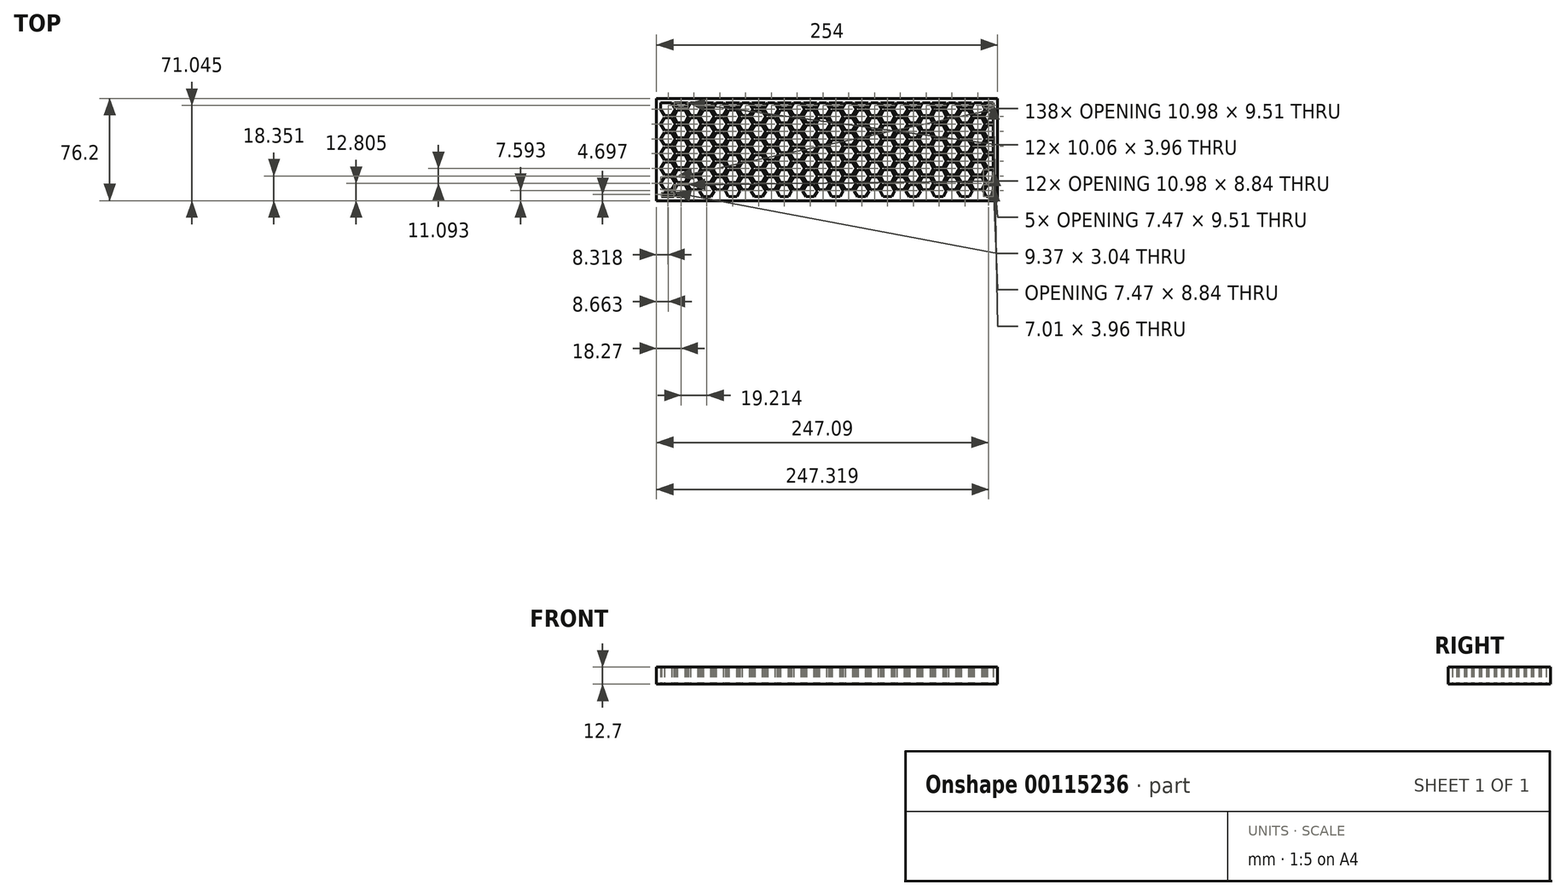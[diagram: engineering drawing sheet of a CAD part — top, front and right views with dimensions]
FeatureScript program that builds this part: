
annotation { "Feature Type Name" : "Feature", "Feature Type Description" : "" }
export const myFeature = defineFeature(function(context is Context, id is Id, definition is map)
    precondition{}
    {
        {
            var Q0;
            Q0=qCreatedBy(makeId("Top.planeOp"),FACE);
            var sketch = newSketch(context, id + "F0", { "sketchPlane" : qUnion([Q0])});
            skLineSegment(sketch, "E0.bottom", {"start": v(0, 0) * mm, "end": v(254, 0) * mm});
            skLineSegment(sketch, "E0.top", {"start": v(0, 76.2) * mm, "end": v(254, 76.2) * mm});
            skLineSegment(sketch, "E0.left", {"start": v(0, 0) * mm, "end": v(0, 76.2) * mm});
            skLineSegment(sketch, "E0.right", {"start": v(254, 0) * mm, "end": v(254, 76.2) * mm});
            skLineSegment(sketch, "E1.0", {"start": v(3.17, 73.02) * mm, "end": v(250.83, 73.02) * mm});
            skLineSegment(sketch, "E1.1", {"start": v(3.17, 3.17) * mm, "end": v(3.17, 73.03) * mm});
            skLineSegment(sketch, "E1.2", {"start": v(3.17, 3.17) * mm, "end": v(250.83, 3.17) * mm});
            skLineSegment(sketch, "E1.3", {"start": v(250.83, 3.17) * mm, "end": v(250.83, 73.03) * mm});
            skCircle(sketch, "E2.cCircle", {"center": v(8.66, 68.27) * mm, "radius": 4.75 * mm, "construction": true});
            skLineSegment(sketch, "E2.0", {"start": v(5.92, 73.02) * mm, "end": v(11.4, 73.02) * mm});
            skLineSegment(sketch, "E2.1", {"start": v(11.4, 73.02) * mm, "end": v(14.15, 68.27) * mm});
            skLineSegment(sketch, "E2.2", {"start": v(14.15, 68.27) * mm, "end": v(11.4, 63.52) * mm});
            skLineSegment(sketch, "E2.3", {"start": v(11.4, 63.52) * mm, "end": v(5.92, 63.52) * mm});
            skLineSegment(sketch, "E2.4", {"start": v(5.92, 63.52) * mm, "end": v(3.17, 68.27) * mm});
            skLineSegment(sketch, "E2.5", {"start": v(3.18, 68.27) * mm, "end": v(5.92, 73.02) * mm});
            skPoint(sketch, "E2.0.midPoint", {"position": v(8.66, 73.03) * mm});
            skPoint(sketch, "E3.0.midPoint", {"position": v(8.6, 62.03) * mm});
            skPoint(sketch, "E4.0.midPoint", {"position": v(12.97, 60.07) * mm});
            skCircle(sketch, "E5.cCircle", {"center": v(18.27, 62.73) * mm, "radius": 4.75 * mm, "construction": true});
            skLineSegment(sketch, "E5.0", {"start": v(15.53, 67.48) * mm, "end": v(21.01, 67.48) * mm});
            skLineSegment(sketch, "E5.1", {"start": v(21.01, 67.48) * mm, "end": v(23.76, 62.73) * mm});
            skLineSegment(sketch, "E5.2", {"start": v(23.76, 62.73) * mm, "end": v(21.01, 57.97) * mm});
            skLineSegment(sketch, "E5.3", {"start": v(21.01, 57.97) * mm, "end": v(15.53, 57.97) * mm});
            skLineSegment(sketch, "E5.4", {"start": v(15.53, 57.97) * mm, "end": v(12.78, 62.73) * mm});
            skLineSegment(sketch, "E5.5", {"start": v(12.78, 62.73) * mm, "end": v(15.53, 67.48) * mm});
            skPoint(sketch, "E5.0.midPoint", {"position": v(18.27, 67.48) * mm});
            skLineSegment(sketch, "E6.0.1.0", {"start": v(11.4, 61.93) * mm, "end": v(14.15, 57.18) * mm});
            skLineSegment(sketch, "E6.0.1.1", {"start": v(3.17, 57.18) * mm, "end": v(5.92, 61.93) * mm});
            skLineSegment(sketch, "E6.0.1.2", {"start": v(5.92, 52.43) * mm, "end": v(3.18, 57.18) * mm});
            skLineSegment(sketch, "E6.0.1.3", {"start": v(11.4, 52.43) * mm, "end": v(5.92, 52.43) * mm});
            skLineSegment(sketch, "E6.0.1.4", {"start": v(14.15, 57.18) * mm, "end": v(11.4, 52.43) * mm});
            skLineSegment(sketch, "E6.0.1.5", {"start": v(12.78, 51.63) * mm, "end": v(15.53, 56.38) * mm});
            skLineSegment(sketch, "E6.0.1.6", {"start": v(15.53, 46.88) * mm, "end": v(12.78, 51.63) * mm});
            skLineSegment(sketch, "E6.0.1.7", {"start": v(21.01, 46.88) * mm, "end": v(15.53, 46.88) * mm});
            skLineSegment(sketch, "E6.0.1.8", {"start": v(23.76, 51.63) * mm, "end": v(21.01, 46.88) * mm});
            skLineSegment(sketch, "E6.0.1.9", {"start": v(21.01, 56.38) * mm, "end": v(23.76, 51.63) * mm});
            skLineSegment(sketch, "E6.0.1.10", {"start": v(15.53, 56.38) * mm, "end": v(21.01, 56.38) * mm});
            skLineSegment(sketch, "E6.0.1.11", {"start": v(5.92, 61.93) * mm, "end": v(11.4, 61.93) * mm});
            skLineSegment(sketch, "E6.0.2.0", {"start": v(11.4, 50.84) * mm, "end": v(14.15, 46.09) * mm});
            skLineSegment(sketch, "E6.0.2.1", {"start": v(3.17, 46.09) * mm, "end": v(5.92, 50.84) * mm});
            skLineSegment(sketch, "E6.0.2.2", {"start": v(5.92, 41.33) * mm, "end": v(3.18, 46.09) * mm});
            skLineSegment(sketch, "E6.0.2.3", {"start": v(11.4, 41.33) * mm, "end": v(5.92, 41.33) * mm});
            skLineSegment(sketch, "E6.0.2.4", {"start": v(14.15, 46.09) * mm, "end": v(11.4, 41.33) * mm});
            skLineSegment(sketch, "E6.0.2.5", {"start": v(12.78, 40.54) * mm, "end": v(15.53, 45.3) * mm});
            skLineSegment(sketch, "E6.0.2.6", {"start": v(15.53, 35.79) * mm, "end": v(12.78, 40.54) * mm});
            skLineSegment(sketch, "E6.0.2.7", {"start": v(21.01, 35.79) * mm, "end": v(15.53, 35.79) * mm});
            skLineSegment(sketch, "E6.0.2.8", {"start": v(23.76, 40.54) * mm, "end": v(21.01, 35.79) * mm});
            skLineSegment(sketch, "E6.0.2.9", {"start": v(21.01, 45.3) * mm, "end": v(23.76, 40.54) * mm});
            skLineSegment(sketch, "E6.0.2.10", {"start": v(15.53, 45.3) * mm, "end": v(21.01, 45.3) * mm});
            skLineSegment(sketch, "E6.0.2.11", {"start": v(5.92, 50.84) * mm, "end": v(11.4, 50.84) * mm});
            skLineSegment(sketch, "E6.0.3.0", {"start": v(11.4, 39.74) * mm, "end": v(14.15, 35) * mm});
            skLineSegment(sketch, "E6.0.3.1", {"start": v(3.17, 35) * mm, "end": v(5.92, 39.74) * mm});
            skLineSegment(sketch, "E6.0.3.2", {"start": v(5.92, 30.24) * mm, "end": v(3.18, 35) * mm});
            skLineSegment(sketch, "E6.0.3.3", {"start": v(11.4, 30.24) * mm, "end": v(5.92, 30.24) * mm});
            skLineSegment(sketch, "E6.0.3.4", {"start": v(14.15, 35) * mm, "end": v(11.4, 30.24) * mm});
            skLineSegment(sketch, "E6.0.3.5", {"start": v(12.78, 29.44) * mm, "end": v(15.53, 34.2) * mm});
            skLineSegment(sketch, "E6.0.3.6", {"start": v(15.53, 24.7) * mm, "end": v(12.78, 29.44) * mm});
            skLineSegment(sketch, "E6.0.3.7", {"start": v(21.01, 24.7) * mm, "end": v(15.53, 24.7) * mm});
            skLineSegment(sketch, "E6.0.3.8", {"start": v(23.76, 29.44) * mm, "end": v(21.01, 24.7) * mm});
            skLineSegment(sketch, "E6.0.3.9", {"start": v(21.01, 34.2) * mm, "end": v(23.76, 29.44) * mm});
            skLineSegment(sketch, "E6.0.3.10", {"start": v(15.53, 34.2) * mm, "end": v(21.01, 34.2) * mm});
            skLineSegment(sketch, "E6.0.3.11", {"start": v(5.92, 39.74) * mm, "end": v(11.4, 39.74) * mm});
            skLineSegment(sketch, "E6.0.4.0", {"start": v(11.4, 28.65) * mm, "end": v(14.15, 23.9) * mm});
            skLineSegment(sketch, "E6.0.4.1", {"start": v(3.17, 23.9) * mm, "end": v(5.92, 28.65) * mm});
            skLineSegment(sketch, "E6.0.4.2", {"start": v(5.92, 19.15) * mm, "end": v(3.18, 23.9) * mm});
            skLineSegment(sketch, "E6.0.4.3", {"start": v(11.4, 19.15) * mm, "end": v(5.92, 19.15) * mm});
            skLineSegment(sketch, "E6.0.4.4", {"start": v(14.15, 23.9) * mm, "end": v(11.4, 19.15) * mm});
            skLineSegment(sketch, "E6.0.4.5", {"start": v(12.78, 18.35) * mm, "end": v(15.53, 23.1) * mm});
            skLineSegment(sketch, "E6.0.4.6", {"start": v(15.53, 13.6) * mm, "end": v(12.78, 18.35) * mm});
            skLineSegment(sketch, "E6.0.4.7", {"start": v(21.01, 13.6) * mm, "end": v(15.53, 13.6) * mm});
            skLineSegment(sketch, "E6.0.4.8", {"start": v(23.76, 18.35) * mm, "end": v(21.01, 13.6) * mm});
            skLineSegment(sketch, "E6.0.4.9", {"start": v(21.01, 23.1) * mm, "end": v(23.76, 18.35) * mm});
            skLineSegment(sketch, "E6.0.4.10", {"start": v(15.53, 23.1) * mm, "end": v(21.01, 23.1) * mm});
            skLineSegment(sketch, "E6.0.4.11", {"start": v(5.92, 28.65) * mm, "end": v(11.4, 28.65) * mm});
            skLineSegment(sketch, "E6.0.5.0", {"start": v(11.4, 17.56) * mm, "end": v(14.15, 12.8) * mm});
            skLineSegment(sketch, "E6.0.5.1", {"start": v(3.18, 12.8) * mm, "end": v(5.92, 17.56) * mm});
            skLineSegment(sketch, "E6.0.5.2", {"start": v(5.92, 8.05) * mm, "end": v(3.18, 12.8) * mm});
            skLineSegment(sketch, "E6.0.5.3", {"start": v(11.4, 8.05) * mm, "end": v(5.92, 8.05) * mm});
            skLineSegment(sketch, "E6.0.5.4", {"start": v(14.15, 12.8) * mm, "end": v(11.4, 8.05) * mm});
            skLineSegment(sketch, "E6.0.5.5", {"start": v(12.78, 7.26) * mm, "end": v(15.53, 12.01) * mm});
            skLineSegment(sketch, "E6.0.5.6", {"start": v(15.53, 2.5) * mm, "end": v(12.78, 7.26) * mm});
            skLineSegment(sketch, "E6.0.5.7", {"start": v(21.01, 2.5) * mm, "end": v(15.53, 2.5) * mm});
            skLineSegment(sketch, "E6.0.5.8", {"start": v(23.76, 7.26) * mm, "end": v(21.01, 2.5) * mm});
            skLineSegment(sketch, "E6.0.5.9", {"start": v(21.01, 12.01) * mm, "end": v(23.76, 7.26) * mm});
            skLineSegment(sketch, "E6.0.5.10", {"start": v(15.53, 12.01) * mm, "end": v(21.01, 12.01) * mm});
            skLineSegment(sketch, "E6.0.5.11", {"start": v(5.92, 17.56) * mm, "end": v(11.4, 17.56) * mm});
            skLineSegment(sketch, "E6.1.0.0", {"start": v(30.62, 73.02) * mm, "end": v(33.37, 68.27) * mm});
            skLineSegment(sketch, "E6.1.0.1", {"start": v(22.39, 68.27) * mm, "end": v(25.13, 73.02) * mm});
            skLineSegment(sketch, "E6.1.0.2", {"start": v(25.13, 63.52) * mm, "end": v(22.39, 68.27) * mm});
            skLineSegment(sketch, "E6.1.0.3", {"start": v(30.62, 63.52) * mm, "end": v(25.13, 63.52) * mm});
            skLineSegment(sketch, "E6.1.0.4", {"start": v(33.37, 68.27) * mm, "end": v(30.62, 63.52) * mm});
            skLineSegment(sketch, "E6.1.0.5", {"start": v(32, 62.73) * mm, "end": v(34.74, 67.48) * mm});
            skLineSegment(sketch, "E6.1.0.6", {"start": v(34.74, 57.97) * mm, "end": v(32, 62.73) * mm});
            skLineSegment(sketch, "E6.1.0.7", {"start": v(40.23, 57.97) * mm, "end": v(34.74, 57.97) * mm});
            skLineSegment(sketch, "E6.1.0.8", {"start": v(42.97, 62.73) * mm, "end": v(40.23, 57.97) * mm});
            skLineSegment(sketch, "E6.1.0.9", {"start": v(40.23, 67.48) * mm, "end": v(42.97, 62.73) * mm});
            skLineSegment(sketch, "E6.1.0.10", {"start": v(34.74, 67.48) * mm, "end": v(40.23, 67.48) * mm});
            skLineSegment(sketch, "E6.1.0.11", {"start": v(25.13, 73.03) * mm, "end": v(30.62, 73.03) * mm});
            skLineSegment(sketch, "E6.1.1.0", {"start": v(30.62, 61.93) * mm, "end": v(33.37, 57.18) * mm});
            skLineSegment(sketch, "E6.1.1.1", {"start": v(22.39, 57.18) * mm, "end": v(25.13, 61.93) * mm});
            skLineSegment(sketch, "E6.1.1.2", {"start": v(25.13, 52.43) * mm, "end": v(22.39, 57.18) * mm});
            skLineSegment(sketch, "E6.1.1.3", {"start": v(30.62, 52.43) * mm, "end": v(25.13, 52.43) * mm});
            skLineSegment(sketch, "E6.1.1.4", {"start": v(33.37, 57.18) * mm, "end": v(30.62, 52.43) * mm});
            skLineSegment(sketch, "E6.1.1.5", {"start": v(32, 51.63) * mm, "end": v(34.74, 56.38) * mm});
            skLineSegment(sketch, "E6.1.1.6", {"start": v(34.74, 46.88) * mm, "end": v(32, 51.63) * mm});
            skLineSegment(sketch, "E6.1.1.7", {"start": v(40.23, 46.88) * mm, "end": v(34.74, 46.88) * mm});
            skLineSegment(sketch, "E6.1.1.8", {"start": v(42.97, 51.63) * mm, "end": v(40.23, 46.88) * mm});
            skLineSegment(sketch, "E6.1.1.9", {"start": v(40.23, 56.38) * mm, "end": v(42.97, 51.63) * mm});
            skLineSegment(sketch, "E6.1.1.10", {"start": v(34.74, 56.38) * mm, "end": v(40.23, 56.38) * mm});
            skLineSegment(sketch, "E6.1.1.11", {"start": v(25.13, 61.93) * mm, "end": v(30.62, 61.93) * mm});
            skLineSegment(sketch, "E6.1.2.0", {"start": v(30.62, 50.84) * mm, "end": v(33.37, 46.09) * mm});
            skLineSegment(sketch, "E6.1.2.1", {"start": v(22.39, 46.09) * mm, "end": v(25.13, 50.84) * mm});
            skLineSegment(sketch, "E6.1.2.2", {"start": v(25.13, 41.33) * mm, "end": v(22.39, 46.09) * mm});
            skLineSegment(sketch, "E6.1.2.3", {"start": v(30.62, 41.33) * mm, "end": v(25.13, 41.33) * mm});
            skLineSegment(sketch, "E6.1.2.4", {"start": v(33.37, 46.09) * mm, "end": v(30.62, 41.33) * mm});
            skLineSegment(sketch, "E6.1.2.5", {"start": v(32, 40.54) * mm, "end": v(34.74, 45.3) * mm});
            skLineSegment(sketch, "E6.1.2.6", {"start": v(34.74, 35.79) * mm, "end": v(32, 40.54) * mm});
            skLineSegment(sketch, "E6.1.2.7", {"start": v(40.23, 35.79) * mm, "end": v(34.74, 35.79) * mm});
            skLineSegment(sketch, "E6.1.2.8", {"start": v(42.97, 40.54) * mm, "end": v(40.23, 35.79) * mm});
            skLineSegment(sketch, "E6.1.2.9", {"start": v(40.23, 45.3) * mm, "end": v(42.97, 40.54) * mm});
            skLineSegment(sketch, "E6.1.2.10", {"start": v(34.74, 45.3) * mm, "end": v(40.23, 45.3) * mm});
            skLineSegment(sketch, "E6.1.2.11", {"start": v(25.13, 50.84) * mm, "end": v(30.62, 50.84) * mm});
            skLineSegment(sketch, "E6.1.3.0", {"start": v(30.62, 39.74) * mm, "end": v(33.37, 35) * mm});
            skLineSegment(sketch, "E6.1.3.1", {"start": v(22.39, 35) * mm, "end": v(25.13, 39.74) * mm});
            skLineSegment(sketch, "E6.1.3.2", {"start": v(25.13, 30.24) * mm, "end": v(22.39, 35) * mm});
            skLineSegment(sketch, "E6.1.3.3", {"start": v(30.62, 30.24) * mm, "end": v(25.13, 30.24) * mm});
            skLineSegment(sketch, "E6.1.3.4", {"start": v(33.37, 35) * mm, "end": v(30.62, 30.24) * mm});
            skLineSegment(sketch, "E6.1.3.5", {"start": v(32, 29.44) * mm, "end": v(34.74, 34.2) * mm});
            skLineSegment(sketch, "E6.1.3.6", {"start": v(34.74, 24.7) * mm, "end": v(32, 29.44) * mm});
            skLineSegment(sketch, "E6.1.3.7", {"start": v(40.23, 24.7) * mm, "end": v(34.74, 24.7) * mm});
            skLineSegment(sketch, "E6.1.3.8", {"start": v(42.97, 29.44) * mm, "end": v(40.23, 24.7) * mm});
            skLineSegment(sketch, "E6.1.3.9", {"start": v(40.23, 34.2) * mm, "end": v(42.97, 29.44) * mm});
            skLineSegment(sketch, "E6.1.3.10", {"start": v(34.74, 34.2) * mm, "end": v(40.23, 34.2) * mm});
            skLineSegment(sketch, "E6.1.3.11", {"start": v(25.13, 39.74) * mm, "end": v(30.62, 39.74) * mm});
            skLineSegment(sketch, "E6.1.4.0", {"start": v(30.62, 28.65) * mm, "end": v(33.37, 23.9) * mm});
            skLineSegment(sketch, "E6.1.4.1", {"start": v(22.39, 23.9) * mm, "end": v(25.13, 28.65) * mm});
            skLineSegment(sketch, "E6.1.4.2", {"start": v(25.13, 19.15) * mm, "end": v(22.39, 23.9) * mm});
            skLineSegment(sketch, "E6.1.4.3", {"start": v(30.62, 19.15) * mm, "end": v(25.13, 19.15) * mm});
            skLineSegment(sketch, "E6.1.4.4", {"start": v(33.37, 23.9) * mm, "end": v(30.62, 19.15) * mm});
            skLineSegment(sketch, "E6.1.4.5", {"start": v(32, 18.35) * mm, "end": v(34.74, 23.1) * mm});
            skLineSegment(sketch, "E6.1.4.6", {"start": v(34.74, 13.6) * mm, "end": v(32, 18.35) * mm});
            skLineSegment(sketch, "E6.1.4.7", {"start": v(40.23, 13.6) * mm, "end": v(34.74, 13.6) * mm});
            skLineSegment(sketch, "E6.1.4.8", {"start": v(42.97, 18.35) * mm, "end": v(40.23, 13.6) * mm});
            skLineSegment(sketch, "E6.1.4.9", {"start": v(40.23, 23.1) * mm, "end": v(42.97, 18.35) * mm});
            skLineSegment(sketch, "E6.1.4.10", {"start": v(34.74, 23.1) * mm, "end": v(40.23, 23.1) * mm});
            skLineSegment(sketch, "E6.1.4.11", {"start": v(25.13, 28.65) * mm, "end": v(30.62, 28.65) * mm});
            skLineSegment(sketch, "E6.1.5.0", {"start": v(30.62, 17.56) * mm, "end": v(33.37, 12.8) * mm});
            skLineSegment(sketch, "E6.1.5.1", {"start": v(22.39, 12.8) * mm, "end": v(25.13, 17.56) * mm});
            skLineSegment(sketch, "E6.1.5.2", {"start": v(25.13, 8.05) * mm, "end": v(22.39, 12.8) * mm});
            skLineSegment(sketch, "E6.1.5.3", {"start": v(30.62, 8.05) * mm, "end": v(25.13, 8.05) * mm});
            skLineSegment(sketch, "E6.1.5.4", {"start": v(33.37, 12.8) * mm, "end": v(30.62, 8.05) * mm});
            skLineSegment(sketch, "E6.1.5.5", {"start": v(32, 7.26) * mm, "end": v(34.74, 12.01) * mm});
            skLineSegment(sketch, "E6.1.5.6", {"start": v(34.74, 2.5) * mm, "end": v(32, 7.26) * mm});
            skLineSegment(sketch, "E6.1.5.7", {"start": v(40.23, 2.5) * mm, "end": v(34.74, 2.5) * mm});
            skLineSegment(sketch, "E6.1.5.8", {"start": v(42.97, 7.26) * mm, "end": v(40.23, 2.5) * mm});
            skLineSegment(sketch, "E6.1.5.9", {"start": v(40.23, 12.01) * mm, "end": v(42.97, 7.26) * mm});
            skLineSegment(sketch, "E6.1.5.10", {"start": v(34.74, 12.01) * mm, "end": v(40.23, 12.01) * mm});
            skLineSegment(sketch, "E6.1.5.11", {"start": v(25.13, 17.56) * mm, "end": v(30.62, 17.56) * mm});
            skLineSegment(sketch, "E6.2.0.0", {"start": v(49.84, 73.02) * mm, "end": v(52.58, 68.27) * mm});
            skLineSegment(sketch, "E6.2.0.1", {"start": v(41.6, 68.27) * mm, "end": v(44.35, 73.02) * mm});
            skLineSegment(sketch, "E6.2.0.2", {"start": v(44.35, 63.52) * mm, "end": v(41.6, 68.27) * mm});
            skLineSegment(sketch, "E6.2.0.3", {"start": v(49.84, 63.52) * mm, "end": v(44.35, 63.52) * mm});
            skLineSegment(sketch, "E6.2.0.4", {"start": v(52.58, 68.27) * mm, "end": v(49.84, 63.52) * mm});
            skLineSegment(sketch, "E6.2.0.5", {"start": v(51.21, 62.73) * mm, "end": v(53.96, 67.48) * mm});
            skLineSegment(sketch, "E6.2.0.6", {"start": v(53.96, 57.97) * mm, "end": v(51.21, 62.73) * mm});
            skLineSegment(sketch, "E6.2.0.7", {"start": v(59.44, 57.97) * mm, "end": v(53.96, 57.97) * mm});
            skLineSegment(sketch, "E6.2.0.8", {"start": v(62.19, 62.73) * mm, "end": v(59.44, 57.97) * mm});
            skLineSegment(sketch, "E6.2.0.9", {"start": v(59.44, 67.48) * mm, "end": v(62.19, 62.73) * mm});
            skLineSegment(sketch, "E6.2.0.10", {"start": v(53.96, 67.48) * mm, "end": v(59.44, 67.48) * mm});
            skLineSegment(sketch, "E6.2.0.11", {"start": v(44.35, 73.03) * mm, "end": v(49.84, 73.03) * mm});
            skLineSegment(sketch, "E6.2.1.0", {"start": v(49.84, 61.93) * mm, "end": v(52.58, 57.18) * mm});
            skLineSegment(sketch, "E6.2.1.1", {"start": v(41.6, 57.18) * mm, "end": v(44.35, 61.93) * mm});
            skLineSegment(sketch, "E6.2.1.2", {"start": v(44.35, 52.43) * mm, "end": v(41.6, 57.18) * mm});
            skLineSegment(sketch, "E6.2.1.3", {"start": v(49.84, 52.43) * mm, "end": v(44.35, 52.43) * mm});
            skLineSegment(sketch, "E6.2.1.4", {"start": v(52.58, 57.18) * mm, "end": v(49.84, 52.43) * mm});
            skLineSegment(sketch, "E6.2.1.5", {"start": v(51.21, 51.63) * mm, "end": v(53.96, 56.38) * mm});
            skLineSegment(sketch, "E6.2.1.6", {"start": v(53.96, 46.88) * mm, "end": v(51.21, 51.63) * mm});
            skLineSegment(sketch, "E6.2.1.7", {"start": v(59.44, 46.88) * mm, "end": v(53.96, 46.88) * mm});
            skLineSegment(sketch, "E6.2.1.8", {"start": v(62.19, 51.63) * mm, "end": v(59.44, 46.88) * mm});
            skLineSegment(sketch, "E6.2.1.9", {"start": v(59.44, 56.38) * mm, "end": v(62.19, 51.63) * mm});
            skLineSegment(sketch, "E6.2.1.10", {"start": v(53.96, 56.38) * mm, "end": v(59.44, 56.38) * mm});
            skLineSegment(sketch, "E6.2.1.11", {"start": v(44.35, 61.93) * mm, "end": v(49.84, 61.93) * mm});
            skLineSegment(sketch, "E6.2.2.0", {"start": v(49.84, 50.84) * mm, "end": v(52.58, 46.09) * mm});
            skLineSegment(sketch, "E6.2.2.1", {"start": v(41.6, 46.09) * mm, "end": v(44.35, 50.84) * mm});
            skLineSegment(sketch, "E6.2.2.2", {"start": v(44.35, 41.33) * mm, "end": v(41.6, 46.09) * mm});
            skLineSegment(sketch, "E6.2.2.3", {"start": v(49.84, 41.33) * mm, "end": v(44.35, 41.33) * mm});
            skLineSegment(sketch, "E6.2.2.4", {"start": v(52.58, 46.09) * mm, "end": v(49.84, 41.33) * mm});
            skLineSegment(sketch, "E6.2.2.5", {"start": v(51.21, 40.54) * mm, "end": v(53.96, 45.3) * mm});
            skLineSegment(sketch, "E6.2.2.6", {"start": v(53.96, 35.79) * mm, "end": v(51.21, 40.54) * mm});
            skLineSegment(sketch, "E6.2.2.7", {"start": v(59.44, 35.79) * mm, "end": v(53.96, 35.79) * mm});
            skLineSegment(sketch, "E6.2.2.8", {"start": v(62.19, 40.54) * mm, "end": v(59.44, 35.79) * mm});
            skLineSegment(sketch, "E6.2.2.9", {"start": v(59.44, 45.3) * mm, "end": v(62.19, 40.54) * mm});
            skLineSegment(sketch, "E6.2.2.10", {"start": v(53.96, 45.3) * mm, "end": v(59.44, 45.3) * mm});
            skLineSegment(sketch, "E6.2.2.11", {"start": v(44.35, 50.84) * mm, "end": v(49.84, 50.84) * mm});
            skLineSegment(sketch, "E6.2.3.0", {"start": v(49.84, 39.74) * mm, "end": v(52.58, 35) * mm});
            skLineSegment(sketch, "E6.2.3.1", {"start": v(41.6, 35) * mm, "end": v(44.35, 39.74) * mm});
            skLineSegment(sketch, "E6.2.3.2", {"start": v(44.35, 30.24) * mm, "end": v(41.6, 35) * mm});
            skLineSegment(sketch, "E6.2.3.3", {"start": v(49.84, 30.24) * mm, "end": v(44.35, 30.24) * mm});
            skLineSegment(sketch, "E6.2.3.4", {"start": v(52.58, 35) * mm, "end": v(49.84, 30.24) * mm});
            skLineSegment(sketch, "E6.2.3.5", {"start": v(51.21, 29.44) * mm, "end": v(53.96, 34.2) * mm});
            skLineSegment(sketch, "E6.2.3.6", {"start": v(53.96, 24.7) * mm, "end": v(51.21, 29.44) * mm});
            skLineSegment(sketch, "E6.2.3.7", {"start": v(59.44, 24.7) * mm, "end": v(53.96, 24.7) * mm});
            skLineSegment(sketch, "E6.2.3.8", {"start": v(62.19, 29.44) * mm, "end": v(59.44, 24.7) * mm});
            skLineSegment(sketch, "E6.2.3.9", {"start": v(59.44, 34.2) * mm, "end": v(62.19, 29.44) * mm});
            skLineSegment(sketch, "E6.2.3.10", {"start": v(53.96, 34.2) * mm, "end": v(59.44, 34.2) * mm});
            skLineSegment(sketch, "E6.2.3.11", {"start": v(44.35, 39.74) * mm, "end": v(49.84, 39.74) * mm});
            skLineSegment(sketch, "E6.2.4.0", {"start": v(49.84, 28.65) * mm, "end": v(52.58, 23.9) * mm});
            skLineSegment(sketch, "E6.2.4.1", {"start": v(41.6, 23.9) * mm, "end": v(44.35, 28.65) * mm});
            skLineSegment(sketch, "E6.2.4.2", {"start": v(44.35, 19.15) * mm, "end": v(41.6, 23.9) * mm});
            skLineSegment(sketch, "E6.2.4.3", {"start": v(49.84, 19.15) * mm, "end": v(44.35, 19.15) * mm});
            skLineSegment(sketch, "E6.2.4.4", {"start": v(52.58, 23.9) * mm, "end": v(49.84, 19.15) * mm});
            skLineSegment(sketch, "E6.2.4.5", {"start": v(51.21, 18.35) * mm, "end": v(53.96, 23.1) * mm});
            skLineSegment(sketch, "E6.2.4.6", {"start": v(53.96, 13.6) * mm, "end": v(51.21, 18.35) * mm});
            skLineSegment(sketch, "E6.2.4.7", {"start": v(59.44, 13.6) * mm, "end": v(53.96, 13.6) * mm});
            skLineSegment(sketch, "E6.2.4.8", {"start": v(62.19, 18.35) * mm, "end": v(59.44, 13.6) * mm});
            skLineSegment(sketch, "E6.2.4.9", {"start": v(59.44, 23.1) * mm, "end": v(62.19, 18.35) * mm});
            skLineSegment(sketch, "E6.2.4.10", {"start": v(53.96, 23.1) * mm, "end": v(59.44, 23.1) * mm});
            skLineSegment(sketch, "E6.2.4.11", {"start": v(44.35, 28.65) * mm, "end": v(49.84, 28.65) * mm});
            skLineSegment(sketch, "E6.2.5.0", {"start": v(49.84, 17.56) * mm, "end": v(52.58, 12.8) * mm});
            skLineSegment(sketch, "E6.2.5.1", {"start": v(41.6, 12.8) * mm, "end": v(44.35, 17.56) * mm});
            skLineSegment(sketch, "E6.2.5.2", {"start": v(44.35, 8.05) * mm, "end": v(41.6, 12.8) * mm});
            skLineSegment(sketch, "E6.2.5.3", {"start": v(49.84, 8.05) * mm, "end": v(44.35, 8.05) * mm});
            skLineSegment(sketch, "E6.2.5.4", {"start": v(52.58, 12.8) * mm, "end": v(49.84, 8.05) * mm});
            skLineSegment(sketch, "E6.2.5.5", {"start": v(51.21, 7.26) * mm, "end": v(53.96, 12.01) * mm});
            skLineSegment(sketch, "E6.2.5.6", {"start": v(53.96, 2.5) * mm, "end": v(51.21, 7.26) * mm});
            skLineSegment(sketch, "E6.2.5.7", {"start": v(59.44, 2.5) * mm, "end": v(53.96, 2.5) * mm});
            skLineSegment(sketch, "E6.2.5.8", {"start": v(62.19, 7.26) * mm, "end": v(59.44, 2.5) * mm});
            skLineSegment(sketch, "E6.2.5.9", {"start": v(59.44, 12.01) * mm, "end": v(62.19, 7.26) * mm});
            skLineSegment(sketch, "E6.2.5.10", {"start": v(53.96, 12.01) * mm, "end": v(59.44, 12.01) * mm});
            skLineSegment(sketch, "E6.2.5.11", {"start": v(44.35, 17.56) * mm, "end": v(49.84, 17.56) * mm});
            skLineSegment(sketch, "E6.3.0.0", {"start": v(69.05, 73.02) * mm, "end": v(71.8, 68.27) * mm});
            skLineSegment(sketch, "E6.3.0.1", {"start": v(60.82, 68.27) * mm, "end": v(63.56, 73.02) * mm});
            skLineSegment(sketch, "E6.3.0.2", {"start": v(63.56, 63.52) * mm, "end": v(60.82, 68.27) * mm});
            skLineSegment(sketch, "E6.3.0.3", {"start": v(69.05, 63.52) * mm, "end": v(63.56, 63.52) * mm});
            skLineSegment(sketch, "E6.3.0.4", {"start": v(71.8, 68.27) * mm, "end": v(69.05, 63.52) * mm});
            skLineSegment(sketch, "E6.3.0.5", {"start": v(70.43, 62.73) * mm, "end": v(73.17, 67.48) * mm});
            skLineSegment(sketch, "E6.3.0.6", {"start": v(73.17, 57.97) * mm, "end": v(70.43, 62.73) * mm});
            skLineSegment(sketch, "E6.3.0.7", {"start": v(78.66, 57.97) * mm, "end": v(73.17, 57.97) * mm});
            skLineSegment(sketch, "E6.3.0.8", {"start": v(81.4, 62.73) * mm, "end": v(78.66, 57.97) * mm});
            skLineSegment(sketch, "E6.3.0.9", {"start": v(78.66, 67.48) * mm, "end": v(81.4, 62.73) * mm});
            skLineSegment(sketch, "E6.3.0.10", {"start": v(73.17, 67.48) * mm, "end": v(78.66, 67.48) * mm});
            skLineSegment(sketch, "E6.3.0.11", {"start": v(63.56, 73.03) * mm, "end": v(69.05, 73.03) * mm});
            skLineSegment(sketch, "E6.3.1.0", {"start": v(69.05, 61.93) * mm, "end": v(71.8, 57.18) * mm});
            skLineSegment(sketch, "E6.3.1.1", {"start": v(60.82, 57.18) * mm, "end": v(63.56, 61.93) * mm});
            skLineSegment(sketch, "E6.3.1.2", {"start": v(63.56, 52.43) * mm, "end": v(60.82, 57.18) * mm});
            skLineSegment(sketch, "E6.3.1.3", {"start": v(69.05, 52.43) * mm, "end": v(63.56, 52.43) * mm});
            skLineSegment(sketch, "E6.3.1.4", {"start": v(71.8, 57.18) * mm, "end": v(69.05, 52.43) * mm});
            skLineSegment(sketch, "E6.3.1.5", {"start": v(70.43, 51.63) * mm, "end": v(73.17, 56.38) * mm});
            skLineSegment(sketch, "E6.3.1.6", {"start": v(73.17, 46.88) * mm, "end": v(70.43, 51.63) * mm});
            skLineSegment(sketch, "E6.3.1.7", {"start": v(78.66, 46.88) * mm, "end": v(73.17, 46.88) * mm});
            skLineSegment(sketch, "E6.3.1.8", {"start": v(81.4, 51.63) * mm, "end": v(78.66, 46.88) * mm});
            skLineSegment(sketch, "E6.3.1.9", {"start": v(78.66, 56.38) * mm, "end": v(81.4, 51.63) * mm});
            skLineSegment(sketch, "E6.3.1.10", {"start": v(73.17, 56.38) * mm, "end": v(78.66, 56.38) * mm});
            skLineSegment(sketch, "E6.3.1.11", {"start": v(63.56, 61.93) * mm, "end": v(69.05, 61.93) * mm});
            skLineSegment(sketch, "E6.3.2.0", {"start": v(69.05, 50.84) * mm, "end": v(71.8, 46.09) * mm});
            skLineSegment(sketch, "E6.3.2.1", {"start": v(60.82, 46.09) * mm, "end": v(63.56, 50.84) * mm});
            skLineSegment(sketch, "E6.3.2.2", {"start": v(63.56, 41.33) * mm, "end": v(60.82, 46.09) * mm});
            skLineSegment(sketch, "E6.3.2.3", {"start": v(69.05, 41.33) * mm, "end": v(63.56, 41.33) * mm});
            skLineSegment(sketch, "E6.3.2.4", {"start": v(71.8, 46.09) * mm, "end": v(69.05, 41.33) * mm});
            skLineSegment(sketch, "E6.3.2.5", {"start": v(70.43, 40.54) * mm, "end": v(73.17, 45.3) * mm});
            skLineSegment(sketch, "E6.3.2.6", {"start": v(73.17, 35.79) * mm, "end": v(70.43, 40.54) * mm});
            skLineSegment(sketch, "E6.3.2.7", {"start": v(78.66, 35.79) * mm, "end": v(73.17, 35.79) * mm});
            skLineSegment(sketch, "E6.3.2.8", {"start": v(81.4, 40.54) * mm, "end": v(78.66, 35.79) * mm});
            skLineSegment(sketch, "E6.3.2.9", {"start": v(78.66, 45.3) * mm, "end": v(81.4, 40.54) * mm});
            skLineSegment(sketch, "E6.3.2.10", {"start": v(73.17, 45.3) * mm, "end": v(78.66, 45.3) * mm});
            skLineSegment(sketch, "E6.3.2.11", {"start": v(63.56, 50.84) * mm, "end": v(69.05, 50.84) * mm});
            skLineSegment(sketch, "E6.3.3.0", {"start": v(69.05, 39.74) * mm, "end": v(71.8, 35) * mm});
            skLineSegment(sketch, "E6.3.3.1", {"start": v(60.82, 35) * mm, "end": v(63.56, 39.74) * mm});
            skLineSegment(sketch, "E6.3.3.2", {"start": v(63.56, 30.24) * mm, "end": v(60.82, 35) * mm});
            skLineSegment(sketch, "E6.3.3.3", {"start": v(69.05, 30.24) * mm, "end": v(63.56, 30.24) * mm});
            skLineSegment(sketch, "E6.3.3.4", {"start": v(71.8, 35) * mm, "end": v(69.05, 30.24) * mm});
            skLineSegment(sketch, "E6.3.3.5", {"start": v(70.43, 29.44) * mm, "end": v(73.17, 34.2) * mm});
            skLineSegment(sketch, "E6.3.3.6", {"start": v(73.17, 24.7) * mm, "end": v(70.43, 29.44) * mm});
            skLineSegment(sketch, "E6.3.3.7", {"start": v(78.66, 24.7) * mm, "end": v(73.17, 24.7) * mm});
            skLineSegment(sketch, "E6.3.3.8", {"start": v(81.4, 29.44) * mm, "end": v(78.66, 24.7) * mm});
            skLineSegment(sketch, "E6.3.3.9", {"start": v(78.66, 34.2) * mm, "end": v(81.4, 29.44) * mm});
            skLineSegment(sketch, "E6.3.3.10", {"start": v(73.17, 34.2) * mm, "end": v(78.66, 34.2) * mm});
            skLineSegment(sketch, "E6.3.3.11", {"start": v(63.56, 39.74) * mm, "end": v(69.05, 39.74) * mm});
            skLineSegment(sketch, "E6.3.4.0", {"start": v(69.05, 28.65) * mm, "end": v(71.8, 23.9) * mm});
            skLineSegment(sketch, "E6.3.4.1", {"start": v(60.82, 23.9) * mm, "end": v(63.56, 28.65) * mm});
            skLineSegment(sketch, "E6.3.4.2", {"start": v(63.56, 19.15) * mm, "end": v(60.82, 23.9) * mm});
            skLineSegment(sketch, "E6.3.4.3", {"start": v(69.05, 19.15) * mm, "end": v(63.56, 19.15) * mm});
            skLineSegment(sketch, "E6.3.4.4", {"start": v(71.8, 23.9) * mm, "end": v(69.05, 19.15) * mm});
            skLineSegment(sketch, "E6.3.4.5", {"start": v(70.43, 18.35) * mm, "end": v(73.17, 23.1) * mm});
            skLineSegment(sketch, "E6.3.4.6", {"start": v(73.17, 13.6) * mm, "end": v(70.43, 18.35) * mm});
            skLineSegment(sketch, "E6.3.4.7", {"start": v(78.66, 13.6) * mm, "end": v(73.17, 13.6) * mm});
            skLineSegment(sketch, "E6.3.4.8", {"start": v(81.4, 18.35) * mm, "end": v(78.66, 13.6) * mm});
            skLineSegment(sketch, "E6.3.4.9", {"start": v(78.66, 23.1) * mm, "end": v(81.4, 18.35) * mm});
            skLineSegment(sketch, "E6.3.4.10", {"start": v(73.17, 23.1) * mm, "end": v(78.66, 23.1) * mm});
            skLineSegment(sketch, "E6.3.4.11", {"start": v(63.56, 28.65) * mm, "end": v(69.05, 28.65) * mm});
            skLineSegment(sketch, "E6.3.5.0", {"start": v(69.05, 17.56) * mm, "end": v(71.8, 12.8) * mm});
            skLineSegment(sketch, "E6.3.5.1", {"start": v(60.82, 12.8) * mm, "end": v(63.56, 17.56) * mm});
            skLineSegment(sketch, "E6.3.5.2", {"start": v(63.56, 8.05) * mm, "end": v(60.82, 12.8) * mm});
            skLineSegment(sketch, "E6.3.5.3", {"start": v(69.05, 8.05) * mm, "end": v(63.56, 8.05) * mm});
            skLineSegment(sketch, "E6.3.5.4", {"start": v(71.8, 12.8) * mm, "end": v(69.05, 8.05) * mm});
            skLineSegment(sketch, "E6.3.5.5", {"start": v(70.43, 7.26) * mm, "end": v(73.17, 12.01) * mm});
            skLineSegment(sketch, "E6.3.5.6", {"start": v(73.17, 2.5) * mm, "end": v(70.43, 7.26) * mm});
            skLineSegment(sketch, "E6.3.5.7", {"start": v(78.66, 2.5) * mm, "end": v(73.17, 2.5) * mm});
            skLineSegment(sketch, "E6.3.5.8", {"start": v(81.4, 7.26) * mm, "end": v(78.66, 2.5) * mm});
            skLineSegment(sketch, "E6.3.5.9", {"start": v(78.66, 12.01) * mm, "end": v(81.4, 7.26) * mm});
            skLineSegment(sketch, "E6.3.5.10", {"start": v(73.17, 12.01) * mm, "end": v(78.66, 12.01) * mm});
            skLineSegment(sketch, "E6.3.5.11", {"start": v(63.56, 17.56) * mm, "end": v(69.05, 17.56) * mm});
            skLineSegment(sketch, "E6.4.0.0", {"start": v(88.27, 73.02) * mm, "end": v(91, 68.27) * mm});
            skLineSegment(sketch, "E6.4.0.1", {"start": v(80.03, 68.27) * mm, "end": v(82.78, 73.02) * mm});
            skLineSegment(sketch, "E6.4.0.2", {"start": v(82.78, 63.52) * mm, "end": v(80.03, 68.27) * mm});
            skLineSegment(sketch, "E6.4.0.3", {"start": v(88.27, 63.52) * mm, "end": v(82.78, 63.52) * mm});
            skLineSegment(sketch, "E6.4.0.4", {"start": v(91, 68.27) * mm, "end": v(88.27, 63.52) * mm});
            skLineSegment(sketch, "E6.4.0.5", {"start": v(89.64, 62.73) * mm, "end": v(92.38, 67.48) * mm});
            skLineSegment(sketch, "E6.4.0.6", {"start": v(92.38, 57.97) * mm, "end": v(89.64, 62.73) * mm});
            skLineSegment(sketch, "E6.4.0.7", {"start": v(97.87, 57.97) * mm, "end": v(92.38, 57.97) * mm});
            skLineSegment(sketch, "E6.4.0.8", {"start": v(100.62, 62.73) * mm, "end": v(97.87, 57.97) * mm});
            skLineSegment(sketch, "E6.4.0.9", {"start": v(97.87, 67.48) * mm, "end": v(100.62, 62.73) * mm});
            skLineSegment(sketch, "E6.4.0.10", {"start": v(92.38, 67.48) * mm, "end": v(97.87, 67.48) * mm});
            skLineSegment(sketch, "E6.4.0.11", {"start": v(82.78, 73.03) * mm, "end": v(88.27, 73.03) * mm});
            skLineSegment(sketch, "E6.4.1.0", {"start": v(88.27, 61.93) * mm, "end": v(91, 57.18) * mm});
            skLineSegment(sketch, "E6.4.1.1", {"start": v(80.03, 57.18) * mm, "end": v(82.78, 61.93) * mm});
            skLineSegment(sketch, "E6.4.1.2", {"start": v(82.78, 52.43) * mm, "end": v(80.03, 57.18) * mm});
            skLineSegment(sketch, "E6.4.1.3", {"start": v(88.27, 52.43) * mm, "end": v(82.78, 52.43) * mm});
            skLineSegment(sketch, "E6.4.1.4", {"start": v(91, 57.18) * mm, "end": v(88.27, 52.43) * mm});
            skLineSegment(sketch, "E6.4.1.5", {"start": v(89.64, 51.63) * mm, "end": v(92.38, 56.38) * mm});
            skLineSegment(sketch, "E6.4.1.6", {"start": v(92.38, 46.88) * mm, "end": v(89.64, 51.63) * mm});
            skLineSegment(sketch, "E6.4.1.7", {"start": v(97.87, 46.88) * mm, "end": v(92.38, 46.88) * mm});
            skLineSegment(sketch, "E6.4.1.8", {"start": v(100.62, 51.63) * mm, "end": v(97.87, 46.88) * mm});
            skLineSegment(sketch, "E6.4.1.9", {"start": v(97.87, 56.38) * mm, "end": v(100.62, 51.63) * mm});
            skLineSegment(sketch, "E6.4.1.10", {"start": v(92.38, 56.38) * mm, "end": v(97.87, 56.38) * mm});
            skLineSegment(sketch, "E6.4.1.11", {"start": v(82.78, 61.93) * mm, "end": v(88.27, 61.93) * mm});
            skLineSegment(sketch, "E6.4.2.0", {"start": v(88.27, 50.84) * mm, "end": v(91, 46.09) * mm});
            skLineSegment(sketch, "E6.4.2.1", {"start": v(80.03, 46.09) * mm, "end": v(82.78, 50.84) * mm});
            skLineSegment(sketch, "E6.4.2.2", {"start": v(82.78, 41.33) * mm, "end": v(80.03, 46.09) * mm});
            skLineSegment(sketch, "E6.4.2.3", {"start": v(88.27, 41.33) * mm, "end": v(82.78, 41.33) * mm});
            skLineSegment(sketch, "E6.4.2.4", {"start": v(91, 46.09) * mm, "end": v(88.27, 41.33) * mm});
            skLineSegment(sketch, "E6.4.2.5", {"start": v(89.64, 40.54) * mm, "end": v(92.38, 45.3) * mm});
            skLineSegment(sketch, "E6.4.2.6", {"start": v(92.38, 35.79) * mm, "end": v(89.64, 40.54) * mm});
            skLineSegment(sketch, "E6.4.2.7", {"start": v(97.87, 35.79) * mm, "end": v(92.38, 35.79) * mm});
            skLineSegment(sketch, "E6.4.2.8", {"start": v(100.62, 40.54) * mm, "end": v(97.87, 35.79) * mm});
            skLineSegment(sketch, "E6.4.2.9", {"start": v(97.87, 45.3) * mm, "end": v(100.62, 40.54) * mm});
            skLineSegment(sketch, "E6.4.2.10", {"start": v(92.38, 45.3) * mm, "end": v(97.87, 45.3) * mm});
            skLineSegment(sketch, "E6.4.2.11", {"start": v(82.78, 50.84) * mm, "end": v(88.27, 50.84) * mm});
            skLineSegment(sketch, "E6.4.3.0", {"start": v(88.27, 39.74) * mm, "end": v(91, 35) * mm});
            skLineSegment(sketch, "E6.4.3.1", {"start": v(80.03, 35) * mm, "end": v(82.78, 39.74) * mm});
            skLineSegment(sketch, "E6.4.3.2", {"start": v(82.78, 30.24) * mm, "end": v(80.03, 35) * mm});
            skLineSegment(sketch, "E6.4.3.3", {"start": v(88.27, 30.24) * mm, "end": v(82.78, 30.24) * mm});
            skLineSegment(sketch, "E6.4.3.4", {"start": v(91, 35) * mm, "end": v(88.27, 30.24) * mm});
            skLineSegment(sketch, "E6.4.3.5", {"start": v(89.64, 29.44) * mm, "end": v(92.38, 34.2) * mm});
            skLineSegment(sketch, "E6.4.3.6", {"start": v(92.38, 24.7) * mm, "end": v(89.64, 29.44) * mm});
            skLineSegment(sketch, "E6.4.3.7", {"start": v(97.87, 24.7) * mm, "end": v(92.38, 24.7) * mm});
            skLineSegment(sketch, "E6.4.3.8", {"start": v(100.62, 29.44) * mm, "end": v(97.87, 24.7) * mm});
            skLineSegment(sketch, "E6.4.3.9", {"start": v(97.87, 34.2) * mm, "end": v(100.62, 29.44) * mm});
            skLineSegment(sketch, "E6.4.3.10", {"start": v(92.38, 34.2) * mm, "end": v(97.87, 34.2) * mm});
            skLineSegment(sketch, "E6.4.3.11", {"start": v(82.78, 39.74) * mm, "end": v(88.27, 39.74) * mm});
            skLineSegment(sketch, "E6.4.4.0", {"start": v(88.27, 28.65) * mm, "end": v(91, 23.9) * mm});
            skLineSegment(sketch, "E6.4.4.1", {"start": v(80.03, 23.9) * mm, "end": v(82.78, 28.65) * mm});
            skLineSegment(sketch, "E6.4.4.2", {"start": v(82.78, 19.15) * mm, "end": v(80.03, 23.9) * mm});
            skLineSegment(sketch, "E6.4.4.3", {"start": v(88.27, 19.15) * mm, "end": v(82.78, 19.15) * mm});
            skLineSegment(sketch, "E6.4.4.4", {"start": v(91, 23.9) * mm, "end": v(88.27, 19.15) * mm});
            skLineSegment(sketch, "E6.4.4.5", {"start": v(89.64, 18.35) * mm, "end": v(92.38, 23.1) * mm});
            skLineSegment(sketch, "E6.4.4.6", {"start": v(92.38, 13.6) * mm, "end": v(89.64, 18.35) * mm});
            skLineSegment(sketch, "E6.4.4.7", {"start": v(97.87, 13.6) * mm, "end": v(92.38, 13.6) * mm});
            skLineSegment(sketch, "E6.4.4.8", {"start": v(100.62, 18.35) * mm, "end": v(97.87, 13.6) * mm});
            skLineSegment(sketch, "E6.4.4.9", {"start": v(97.87, 23.1) * mm, "end": v(100.62, 18.35) * mm});
            skLineSegment(sketch, "E6.4.4.10", {"start": v(92.38, 23.1) * mm, "end": v(97.87, 23.1) * mm});
            skLineSegment(sketch, "E6.4.4.11", {"start": v(82.78, 28.65) * mm, "end": v(88.27, 28.65) * mm});
            skLineSegment(sketch, "E6.4.5.0", {"start": v(88.27, 17.56) * mm, "end": v(91, 12.8) * mm});
            skLineSegment(sketch, "E6.4.5.1", {"start": v(80.03, 12.8) * mm, "end": v(82.78, 17.56) * mm});
            skLineSegment(sketch, "E6.4.5.2", {"start": v(82.78, 8.05) * mm, "end": v(80.03, 12.8) * mm});
            skLineSegment(sketch, "E6.4.5.3", {"start": v(88.27, 8.05) * mm, "end": v(82.78, 8.05) * mm});
            skLineSegment(sketch, "E6.4.5.4", {"start": v(91, 12.8) * mm, "end": v(88.27, 8.05) * mm});
            skLineSegment(sketch, "E6.4.5.5", {"start": v(89.64, 7.26) * mm, "end": v(92.38, 12.01) * mm});
            skLineSegment(sketch, "E6.4.5.6", {"start": v(92.38, 2.5) * mm, "end": v(89.64, 7.26) * mm});
            skLineSegment(sketch, "E6.4.5.7", {"start": v(97.87, 2.5) * mm, "end": v(92.38, 2.5) * mm});
            skLineSegment(sketch, "E6.4.5.8", {"start": v(100.62, 7.26) * mm, "end": v(97.87, 2.5) * mm});
            skLineSegment(sketch, "E6.4.5.9", {"start": v(97.87, 12.01) * mm, "end": v(100.62, 7.26) * mm});
            skLineSegment(sketch, "E6.4.5.10", {"start": v(92.38, 12.01) * mm, "end": v(97.87, 12.01) * mm});
            skLineSegment(sketch, "E6.4.5.11", {"start": v(82.78, 17.56) * mm, "end": v(88.27, 17.56) * mm});
            skLineSegment(sketch, "E6.5.0.0", {"start": v(107.48, 73.02) * mm, "end": v(110.22, 68.27) * mm});
            skLineSegment(sketch, "E6.5.0.1", {"start": v(99.25, 68.27) * mm, "end": v(102, 73.02) * mm});
            skLineSegment(sketch, "E6.5.0.2", {"start": v(102, 63.52) * mm, "end": v(99.25, 68.27) * mm});
            skLineSegment(sketch, "E6.5.0.3", {"start": v(107.48, 63.52) * mm, "end": v(102, 63.52) * mm});
            skLineSegment(sketch, "E6.5.0.4", {"start": v(110.22, 68.27) * mm, "end": v(107.48, 63.52) * mm});
            skLineSegment(sketch, "E6.5.0.5", {"start": v(108.85, 62.73) * mm, "end": v(111.6, 67.48) * mm});
            skLineSegment(sketch, "E6.5.0.6", {"start": v(111.6, 57.97) * mm, "end": v(108.85, 62.73) * mm});
            skLineSegment(sketch, "E6.5.0.7", {"start": v(117.09, 57.97) * mm, "end": v(111.6, 57.97) * mm});
            skLineSegment(sketch, "E6.5.0.8", {"start": v(119.83, 62.73) * mm, "end": v(117.09, 57.97) * mm});
            skLineSegment(sketch, "E6.5.0.9", {"start": v(117.09, 67.48) * mm, "end": v(119.83, 62.73) * mm});
            skLineSegment(sketch, "E6.5.0.10", {"start": v(111.6, 67.48) * mm, "end": v(117.09, 67.48) * mm});
            skLineSegment(sketch, "E6.5.0.11", {"start": v(102, 73.03) * mm, "end": v(107.48, 73.03) * mm});
            skLineSegment(sketch, "E6.5.1.0", {"start": v(107.48, 61.93) * mm, "end": v(110.22, 57.18) * mm});
            skLineSegment(sketch, "E6.5.1.1", {"start": v(99.25, 57.18) * mm, "end": v(102, 61.93) * mm});
            skLineSegment(sketch, "E6.5.1.2", {"start": v(102, 52.43) * mm, "end": v(99.25, 57.18) * mm});
            skLineSegment(sketch, "E6.5.1.3", {"start": v(107.48, 52.43) * mm, "end": v(102, 52.43) * mm});
            skLineSegment(sketch, "E6.5.1.4", {"start": v(110.22, 57.18) * mm, "end": v(107.48, 52.43) * mm});
            skLineSegment(sketch, "E6.5.1.5", {"start": v(108.85, 51.63) * mm, "end": v(111.6, 56.38) * mm});
            skLineSegment(sketch, "E6.5.1.6", {"start": v(111.6, 46.88) * mm, "end": v(108.85, 51.63) * mm});
            skLineSegment(sketch, "E6.5.1.7", {"start": v(117.09, 46.88) * mm, "end": v(111.6, 46.88) * mm});
            skLineSegment(sketch, "E6.5.1.8", {"start": v(119.83, 51.63) * mm, "end": v(117.09, 46.88) * mm});
            skLineSegment(sketch, "E6.5.1.9", {"start": v(117.09, 56.38) * mm, "end": v(119.83, 51.63) * mm});
            skLineSegment(sketch, "E6.5.1.10", {"start": v(111.6, 56.38) * mm, "end": v(117.09, 56.38) * mm});
            skLineSegment(sketch, "E6.5.1.11", {"start": v(102, 61.93) * mm, "end": v(107.48, 61.93) * mm});
            skLineSegment(sketch, "E6.5.2.0", {"start": v(107.48, 50.84) * mm, "end": v(110.22, 46.09) * mm});
            skLineSegment(sketch, "E6.5.2.1", {"start": v(99.25, 46.09) * mm, "end": v(102, 50.84) * mm});
            skLineSegment(sketch, "E6.5.2.2", {"start": v(102, 41.33) * mm, "end": v(99.25, 46.09) * mm});
            skLineSegment(sketch, "E6.5.2.3", {"start": v(107.48, 41.33) * mm, "end": v(102, 41.33) * mm});
            skLineSegment(sketch, "E6.5.2.4", {"start": v(110.22, 46.09) * mm, "end": v(107.48, 41.33) * mm});
            skLineSegment(sketch, "E6.5.2.5", {"start": v(108.85, 40.54) * mm, "end": v(111.6, 45.3) * mm});
            skLineSegment(sketch, "E6.5.2.6", {"start": v(111.6, 35.79) * mm, "end": v(108.85, 40.54) * mm});
            skLineSegment(sketch, "E6.5.2.7", {"start": v(117.09, 35.79) * mm, "end": v(111.6, 35.79) * mm});
            skLineSegment(sketch, "E6.5.2.8", {"start": v(119.83, 40.54) * mm, "end": v(117.09, 35.79) * mm});
            skLineSegment(sketch, "E6.5.2.9", {"start": v(117.09, 45.3) * mm, "end": v(119.83, 40.54) * mm});
            skLineSegment(sketch, "E6.5.2.10", {"start": v(111.6, 45.3) * mm, "end": v(117.09, 45.3) * mm});
            skLineSegment(sketch, "E6.5.2.11", {"start": v(102, 50.84) * mm, "end": v(107.48, 50.84) * mm});
            skLineSegment(sketch, "E6.5.3.0", {"start": v(107.48, 39.74) * mm, "end": v(110.22, 35) * mm});
            skLineSegment(sketch, "E6.5.3.1", {"start": v(99.25, 35) * mm, "end": v(102, 39.74) * mm});
            skLineSegment(sketch, "E6.5.3.2", {"start": v(102, 30.24) * mm, "end": v(99.25, 35) * mm});
            skLineSegment(sketch, "E6.5.3.3", {"start": v(107.48, 30.24) * mm, "end": v(102, 30.24) * mm});
            skLineSegment(sketch, "E6.5.3.4", {"start": v(110.22, 35) * mm, "end": v(107.48, 30.24) * mm});
            skLineSegment(sketch, "E6.5.3.5", {"start": v(108.85, 29.44) * mm, "end": v(111.6, 34.2) * mm});
            skLineSegment(sketch, "E6.5.3.6", {"start": v(111.6, 24.7) * mm, "end": v(108.85, 29.44) * mm});
            skLineSegment(sketch, "E6.5.3.7", {"start": v(117.09, 24.7) * mm, "end": v(111.6, 24.7) * mm});
            skLineSegment(sketch, "E6.5.3.8", {"start": v(119.83, 29.44) * mm, "end": v(117.09, 24.7) * mm});
            skLineSegment(sketch, "E6.5.3.9", {"start": v(117.09, 34.2) * mm, "end": v(119.83, 29.44) * mm});
            skLineSegment(sketch, "E6.5.3.10", {"start": v(111.6, 34.2) * mm, "end": v(117.09, 34.2) * mm});
            skLineSegment(sketch, "E6.5.3.11", {"start": v(102, 39.74) * mm, "end": v(107.48, 39.74) * mm});
            skLineSegment(sketch, "E6.5.4.0", {"start": v(107.48, 28.65) * mm, "end": v(110.22, 23.9) * mm});
            skLineSegment(sketch, "E6.5.4.1", {"start": v(99.25, 23.9) * mm, "end": v(102, 28.65) * mm});
            skLineSegment(sketch, "E6.5.4.2", {"start": v(102, 19.15) * mm, "end": v(99.25, 23.9) * mm});
            skLineSegment(sketch, "E6.5.4.3", {"start": v(107.48, 19.15) * mm, "end": v(102, 19.15) * mm});
            skLineSegment(sketch, "E6.5.4.4", {"start": v(110.22, 23.9) * mm, "end": v(107.48, 19.15) * mm});
            skLineSegment(sketch, "E6.5.4.5", {"start": v(108.85, 18.35) * mm, "end": v(111.6, 23.1) * mm});
            skLineSegment(sketch, "E6.5.4.6", {"start": v(111.6, 13.6) * mm, "end": v(108.85, 18.35) * mm});
            skLineSegment(sketch, "E6.5.4.7", {"start": v(117.09, 13.6) * mm, "end": v(111.6, 13.6) * mm});
            skLineSegment(sketch, "E6.5.4.8", {"start": v(119.83, 18.35) * mm, "end": v(117.09, 13.6) * mm});
            skLineSegment(sketch, "E6.5.4.9", {"start": v(117.09, 23.1) * mm, "end": v(119.83, 18.35) * mm});
            skLineSegment(sketch, "E6.5.4.10", {"start": v(111.6, 23.1) * mm, "end": v(117.09, 23.1) * mm});
            skLineSegment(sketch, "E6.5.4.11", {"start": v(102, 28.65) * mm, "end": v(107.48, 28.65) * mm});
            skLineSegment(sketch, "E6.5.5.0", {"start": v(107.48, 17.56) * mm, "end": v(110.22, 12.8) * mm});
            skLineSegment(sketch, "E6.5.5.1", {"start": v(99.25, 12.8) * mm, "end": v(102, 17.56) * mm});
            skLineSegment(sketch, "E6.5.5.2", {"start": v(102, 8.05) * mm, "end": v(99.25, 12.8) * mm});
            skLineSegment(sketch, "E6.5.5.3", {"start": v(107.48, 8.05) * mm, "end": v(102, 8.05) * mm});
            skLineSegment(sketch, "E6.5.5.4", {"start": v(110.22, 12.8) * mm, "end": v(107.48, 8.05) * mm});
            skLineSegment(sketch, "E6.5.5.5", {"start": v(108.85, 7.26) * mm, "end": v(111.6, 12.01) * mm});
            skLineSegment(sketch, "E6.5.5.6", {"start": v(111.6, 2.5) * mm, "end": v(108.85, 7.26) * mm});
            skLineSegment(sketch, "E6.5.5.7", {"start": v(117.09, 2.5) * mm, "end": v(111.6, 2.5) * mm});
            skLineSegment(sketch, "E6.5.5.8", {"start": v(119.83, 7.26) * mm, "end": v(117.09, 2.5) * mm});
            skLineSegment(sketch, "E6.5.5.9", {"start": v(117.09, 12.01) * mm, "end": v(119.83, 7.26) * mm});
            skLineSegment(sketch, "E6.5.5.10", {"start": v(111.6, 12.01) * mm, "end": v(117.09, 12.01) * mm});
            skLineSegment(sketch, "E6.5.5.11", {"start": v(102, 17.56) * mm, "end": v(107.48, 17.56) * mm});
            skLineSegment(sketch, "E6.6.0.0", {"start": v(126.7, 73.02) * mm, "end": v(129.44, 68.27) * mm});
            skLineSegment(sketch, "E6.6.0.1", {"start": v(118.46, 68.27) * mm, "end": v(121.2, 73.02) * mm});
            skLineSegment(sketch, "E6.6.0.2", {"start": v(121.2, 63.52) * mm, "end": v(118.46, 68.27) * mm});
            skLineSegment(sketch, "E6.6.0.3", {"start": v(126.7, 63.52) * mm, "end": v(121.2, 63.52) * mm});
            skLineSegment(sketch, "E6.6.0.4", {"start": v(129.44, 68.27) * mm, "end": v(126.7, 63.52) * mm});
            skLineSegment(sketch, "E6.6.0.5", {"start": v(128.07, 62.73) * mm, "end": v(130.81, 67.48) * mm});
            skLineSegment(sketch, "E6.6.0.6", {"start": v(130.81, 57.97) * mm, "end": v(128.07, 62.73) * mm});
            skLineSegment(sketch, "E6.6.0.7", {"start": v(136.3, 57.97) * mm, "end": v(130.81, 57.97) * mm});
            skLineSegment(sketch, "E6.6.0.8", {"start": v(139.05, 62.73) * mm, "end": v(136.3, 57.97) * mm});
            skLineSegment(sketch, "E6.6.0.9", {"start": v(136.3, 67.48) * mm, "end": v(139.05, 62.73) * mm});
            skLineSegment(sketch, "E6.6.0.10", {"start": v(130.81, 67.48) * mm, "end": v(136.3, 67.48) * mm});
            skLineSegment(sketch, "E6.6.0.11", {"start": v(121.2, 73.03) * mm, "end": v(126.7, 73.03) * mm});
            skLineSegment(sketch, "E6.6.1.0", {"start": v(126.7, 61.93) * mm, "end": v(129.44, 57.18) * mm});
            skLineSegment(sketch, "E6.6.1.1", {"start": v(118.46, 57.18) * mm, "end": v(121.2, 61.93) * mm});
            skLineSegment(sketch, "E6.6.1.2", {"start": v(121.2, 52.43) * mm, "end": v(118.46, 57.18) * mm});
            skLineSegment(sketch, "E6.6.1.3", {"start": v(126.7, 52.43) * mm, "end": v(121.2, 52.43) * mm});
            skLineSegment(sketch, "E6.6.1.4", {"start": v(129.44, 57.18) * mm, "end": v(126.7, 52.43) * mm});
            skLineSegment(sketch, "E6.6.1.5", {"start": v(128.07, 51.63) * mm, "end": v(130.81, 56.38) * mm});
            skLineSegment(sketch, "E6.6.1.6", {"start": v(130.81, 46.88) * mm, "end": v(128.07, 51.63) * mm});
            skLineSegment(sketch, "E6.6.1.7", {"start": v(136.3, 46.88) * mm, "end": v(130.81, 46.88) * mm});
            skLineSegment(sketch, "E6.6.1.8", {"start": v(139.05, 51.63) * mm, "end": v(136.3, 46.88) * mm});
            skLineSegment(sketch, "E6.6.1.9", {"start": v(136.3, 56.38) * mm, "end": v(139.05, 51.63) * mm});
            skLineSegment(sketch, "E6.6.1.10", {"start": v(130.81, 56.38) * mm, "end": v(136.3, 56.38) * mm});
            skLineSegment(sketch, "E6.6.1.11", {"start": v(121.2, 61.93) * mm, "end": v(126.7, 61.93) * mm});
            skLineSegment(sketch, "E6.6.2.0", {"start": v(126.7, 50.84) * mm, "end": v(129.44, 46.09) * mm});
            skLineSegment(sketch, "E6.6.2.1", {"start": v(118.46, 46.09) * mm, "end": v(121.2, 50.84) * mm});
            skLineSegment(sketch, "E6.6.2.2", {"start": v(121.2, 41.33) * mm, "end": v(118.46, 46.09) * mm});
            skLineSegment(sketch, "E6.6.2.3", {"start": v(126.7, 41.33) * mm, "end": v(121.2, 41.33) * mm});
            skLineSegment(sketch, "E6.6.2.4", {"start": v(129.44, 46.09) * mm, "end": v(126.7, 41.33) * mm});
            skLineSegment(sketch, "E6.6.2.5", {"start": v(128.07, 40.54) * mm, "end": v(130.81, 45.3) * mm});
            skLineSegment(sketch, "E6.6.2.6", {"start": v(130.81, 35.79) * mm, "end": v(128.07, 40.54) * mm});
            skLineSegment(sketch, "E6.6.2.7", {"start": v(136.3, 35.79) * mm, "end": v(130.81, 35.79) * mm});
            skLineSegment(sketch, "E6.6.2.8", {"start": v(139.05, 40.54) * mm, "end": v(136.3, 35.79) * mm});
            skLineSegment(sketch, "E6.6.2.9", {"start": v(136.3, 45.3) * mm, "end": v(139.05, 40.54) * mm});
            skLineSegment(sketch, "E6.6.2.10", {"start": v(130.81, 45.3) * mm, "end": v(136.3, 45.3) * mm});
            skLineSegment(sketch, "E6.6.2.11", {"start": v(121.2, 50.84) * mm, "end": v(126.7, 50.84) * mm});
            skLineSegment(sketch, "E6.6.3.0", {"start": v(126.7, 39.74) * mm, "end": v(129.44, 35) * mm});
            skLineSegment(sketch, "E6.6.3.1", {"start": v(118.46, 35) * mm, "end": v(121.2, 39.74) * mm});
            skLineSegment(sketch, "E6.6.3.2", {"start": v(121.2, 30.24) * mm, "end": v(118.46, 35) * mm});
            skLineSegment(sketch, "E6.6.3.3", {"start": v(126.7, 30.24) * mm, "end": v(121.2, 30.24) * mm});
            skLineSegment(sketch, "E6.6.3.4", {"start": v(129.44, 35) * mm, "end": v(126.7, 30.24) * mm});
            skLineSegment(sketch, "E6.6.3.5", {"start": v(128.07, 29.44) * mm, "end": v(130.81, 34.2) * mm});
            skLineSegment(sketch, "E6.6.3.6", {"start": v(130.81, 24.7) * mm, "end": v(128.07, 29.44) * mm});
            skLineSegment(sketch, "E6.6.3.7", {"start": v(136.3, 24.7) * mm, "end": v(130.81, 24.7) * mm});
            skLineSegment(sketch, "E6.6.3.8", {"start": v(139.05, 29.44) * mm, "end": v(136.3, 24.7) * mm});
            skLineSegment(sketch, "E6.6.3.9", {"start": v(136.3, 34.2) * mm, "end": v(139.05, 29.44) * mm});
            skLineSegment(sketch, "E6.6.3.10", {"start": v(130.81, 34.2) * mm, "end": v(136.3, 34.2) * mm});
            skLineSegment(sketch, "E6.6.3.11", {"start": v(121.2, 39.74) * mm, "end": v(126.7, 39.74) * mm});
            skLineSegment(sketch, "E6.6.4.0", {"start": v(126.7, 28.65) * mm, "end": v(129.44, 23.9) * mm});
            skLineSegment(sketch, "E6.6.4.1", {"start": v(118.46, 23.9) * mm, "end": v(121.2, 28.65) * mm});
            skLineSegment(sketch, "E6.6.4.2", {"start": v(121.2, 19.15) * mm, "end": v(118.46, 23.9) * mm});
            skLineSegment(sketch, "E6.6.4.3", {"start": v(126.7, 19.15) * mm, "end": v(121.2, 19.15) * mm});
            skLineSegment(sketch, "E6.6.4.4", {"start": v(129.44, 23.9) * mm, "end": v(126.7, 19.15) * mm});
            skLineSegment(sketch, "E6.6.4.5", {"start": v(128.07, 18.35) * mm, "end": v(130.81, 23.1) * mm});
            skLineSegment(sketch, "E6.6.4.6", {"start": v(130.81, 13.6) * mm, "end": v(128.07, 18.35) * mm});
            skLineSegment(sketch, "E6.6.4.7", {"start": v(136.3, 13.6) * mm, "end": v(130.81, 13.6) * mm});
            skLineSegment(sketch, "E6.6.4.8", {"start": v(139.05, 18.35) * mm, "end": v(136.3, 13.6) * mm});
            skLineSegment(sketch, "E6.6.4.9", {"start": v(136.3, 23.1) * mm, "end": v(139.05, 18.35) * mm});
            skLineSegment(sketch, "E6.6.4.10", {"start": v(130.81, 23.1) * mm, "end": v(136.3, 23.1) * mm});
            skLineSegment(sketch, "E6.6.4.11", {"start": v(121.2, 28.65) * mm, "end": v(126.7, 28.65) * mm});
            skLineSegment(sketch, "E6.6.5.0", {"start": v(126.7, 17.56) * mm, "end": v(129.44, 12.8) * mm});
            skLineSegment(sketch, "E6.6.5.1", {"start": v(118.46, 12.8) * mm, "end": v(121.2, 17.56) * mm});
            skLineSegment(sketch, "E6.6.5.2", {"start": v(121.2, 8.05) * mm, "end": v(118.46, 12.8) * mm});
            skLineSegment(sketch, "E6.6.5.3", {"start": v(126.7, 8.05) * mm, "end": v(121.2, 8.05) * mm});
            skLineSegment(sketch, "E6.6.5.4", {"start": v(129.44, 12.8) * mm, "end": v(126.7, 8.05) * mm});
            skLineSegment(sketch, "E6.6.5.5", {"start": v(128.07, 7.26) * mm, "end": v(130.81, 12.01) * mm});
            skLineSegment(sketch, "E6.6.5.6", {"start": v(130.81, 2.5) * mm, "end": v(128.07, 7.26) * mm});
            skLineSegment(sketch, "E6.6.5.7", {"start": v(136.3, 2.5) * mm, "end": v(130.81, 2.5) * mm});
            skLineSegment(sketch, "E6.6.5.8", {"start": v(139.05, 7.26) * mm, "end": v(136.3, 2.5) * mm});
            skLineSegment(sketch, "E6.6.5.9", {"start": v(136.3, 12.01) * mm, "end": v(139.05, 7.26) * mm});
            skLineSegment(sketch, "E6.6.5.10", {"start": v(130.81, 12.01) * mm, "end": v(136.3, 12.01) * mm});
            skLineSegment(sketch, "E6.6.5.11", {"start": v(121.2, 17.56) * mm, "end": v(126.7, 17.56) * mm});
            skLineSegment(sketch, "E6.7.0.0", {"start": v(145.9, 73.02) * mm, "end": v(148.65, 68.27) * mm});
            skLineSegment(sketch, "E6.7.0.1", {"start": v(137.68, 68.27) * mm, "end": v(140.42, 73.02) * mm});
            skLineSegment(sketch, "E6.7.0.2", {"start": v(140.42, 63.52) * mm, "end": v(137.68, 68.27) * mm});
            skLineSegment(sketch, "E6.7.0.3", {"start": v(145.9, 63.52) * mm, "end": v(140.42, 63.52) * mm});
            skLineSegment(sketch, "E6.7.0.4", {"start": v(148.65, 68.27) * mm, "end": v(145.9, 63.52) * mm});
            skLineSegment(sketch, "E6.7.0.5", {"start": v(147.28, 62.73) * mm, "end": v(150.03, 67.48) * mm});
            skLineSegment(sketch, "E6.7.0.6", {"start": v(150.03, 57.97) * mm, "end": v(147.28, 62.73) * mm});
            skLineSegment(sketch, "E6.7.0.7", {"start": v(155.52, 57.97) * mm, "end": v(150.03, 57.97) * mm});
            skLineSegment(sketch, "E6.7.0.8", {"start": v(158.26, 62.73) * mm, "end": v(155.52, 57.97) * mm});
            skLineSegment(sketch, "E6.7.0.9", {"start": v(155.52, 67.48) * mm, "end": v(158.26, 62.73) * mm});
            skLineSegment(sketch, "E6.7.0.10", {"start": v(150.03, 67.48) * mm, "end": v(155.52, 67.48) * mm});
            skLineSegment(sketch, "E6.7.0.11", {"start": v(140.42, 73.03) * mm, "end": v(145.9, 73.03) * mm});
            skLineSegment(sketch, "E6.7.1.0", {"start": v(145.9, 61.93) * mm, "end": v(148.65, 57.18) * mm});
            skLineSegment(sketch, "E6.7.1.1", {"start": v(137.68, 57.18) * mm, "end": v(140.42, 61.93) * mm});
            skLineSegment(sketch, "E6.7.1.2", {"start": v(140.42, 52.43) * mm, "end": v(137.68, 57.18) * mm});
            skLineSegment(sketch, "E6.7.1.3", {"start": v(145.9, 52.43) * mm, "end": v(140.42, 52.43) * mm});
            skLineSegment(sketch, "E6.7.1.4", {"start": v(148.65, 57.18) * mm, "end": v(145.9, 52.43) * mm});
            skLineSegment(sketch, "E6.7.1.5", {"start": v(147.28, 51.63) * mm, "end": v(150.03, 56.38) * mm});
            skLineSegment(sketch, "E6.7.1.6", {"start": v(150.03, 46.88) * mm, "end": v(147.28, 51.63) * mm});
            skLineSegment(sketch, "E6.7.1.7", {"start": v(155.52, 46.88) * mm, "end": v(150.03, 46.88) * mm});
            skLineSegment(sketch, "E6.7.1.8", {"start": v(158.26, 51.63) * mm, "end": v(155.52, 46.88) * mm});
            skLineSegment(sketch, "E6.7.1.9", {"start": v(155.52, 56.38) * mm, "end": v(158.26, 51.63) * mm});
            skLineSegment(sketch, "E6.7.1.10", {"start": v(150.03, 56.38) * mm, "end": v(155.52, 56.38) * mm});
            skLineSegment(sketch, "E6.7.1.11", {"start": v(140.42, 61.93) * mm, "end": v(145.9, 61.93) * mm});
            skLineSegment(sketch, "E6.7.2.0", {"start": v(145.9, 50.84) * mm, "end": v(148.65, 46.09) * mm});
            skLineSegment(sketch, "E6.7.2.1", {"start": v(137.68, 46.09) * mm, "end": v(140.42, 50.84) * mm});
            skLineSegment(sketch, "E6.7.2.2", {"start": v(140.42, 41.33) * mm, "end": v(137.68, 46.09) * mm});
            skLineSegment(sketch, "E6.7.2.3", {"start": v(145.9, 41.33) * mm, "end": v(140.42, 41.33) * mm});
            skLineSegment(sketch, "E6.7.2.4", {"start": v(148.65, 46.09) * mm, "end": v(145.9, 41.33) * mm});
            skLineSegment(sketch, "E6.7.2.5", {"start": v(147.28, 40.54) * mm, "end": v(150.03, 45.3) * mm});
            skLineSegment(sketch, "E6.7.2.6", {"start": v(150.03, 35.79) * mm, "end": v(147.28, 40.54) * mm});
            skLineSegment(sketch, "E6.7.2.7", {"start": v(155.52, 35.79) * mm, "end": v(150.03, 35.79) * mm});
            skLineSegment(sketch, "E6.7.2.8", {"start": v(158.26, 40.54) * mm, "end": v(155.52, 35.79) * mm});
            skLineSegment(sketch, "E6.7.2.9", {"start": v(155.52, 45.3) * mm, "end": v(158.26, 40.54) * mm});
            skLineSegment(sketch, "E6.7.2.10", {"start": v(150.03, 45.3) * mm, "end": v(155.52, 45.3) * mm});
            skLineSegment(sketch, "E6.7.2.11", {"start": v(140.42, 50.84) * mm, "end": v(145.9, 50.84) * mm});
            skLineSegment(sketch, "E6.7.3.0", {"start": v(145.9, 39.74) * mm, "end": v(148.65, 35) * mm});
            skLineSegment(sketch, "E6.7.3.1", {"start": v(137.68, 35) * mm, "end": v(140.42, 39.74) * mm});
            skLineSegment(sketch, "E6.7.3.2", {"start": v(140.42, 30.24) * mm, "end": v(137.68, 35) * mm});
            skLineSegment(sketch, "E6.7.3.3", {"start": v(145.9, 30.24) * mm, "end": v(140.42, 30.24) * mm});
            skLineSegment(sketch, "E6.7.3.4", {"start": v(148.65, 35) * mm, "end": v(145.9, 30.24) * mm});
            skLineSegment(sketch, "E6.7.3.5", {"start": v(147.28, 29.44) * mm, "end": v(150.03, 34.2) * mm});
            skLineSegment(sketch, "E6.7.3.6", {"start": v(150.03, 24.7) * mm, "end": v(147.28, 29.44) * mm});
            skLineSegment(sketch, "E6.7.3.7", {"start": v(155.52, 24.7) * mm, "end": v(150.03, 24.7) * mm});
            skLineSegment(sketch, "E6.7.3.8", {"start": v(158.26, 29.44) * mm, "end": v(155.52, 24.7) * mm});
            skLineSegment(sketch, "E6.7.3.9", {"start": v(155.52, 34.2) * mm, "end": v(158.26, 29.44) * mm});
            skLineSegment(sketch, "E6.7.3.10", {"start": v(150.03, 34.2) * mm, "end": v(155.52, 34.2) * mm});
            skLineSegment(sketch, "E6.7.3.11", {"start": v(140.42, 39.74) * mm, "end": v(145.9, 39.74) * mm});
            skLineSegment(sketch, "E6.7.4.0", {"start": v(145.9, 28.65) * mm, "end": v(148.65, 23.9) * mm});
            skLineSegment(sketch, "E6.7.4.1", {"start": v(137.68, 23.9) * mm, "end": v(140.42, 28.65) * mm});
            skLineSegment(sketch, "E6.7.4.2", {"start": v(140.42, 19.15) * mm, "end": v(137.68, 23.9) * mm});
            skLineSegment(sketch, "E6.7.4.3", {"start": v(145.9, 19.15) * mm, "end": v(140.42, 19.15) * mm});
            skLineSegment(sketch, "E6.7.4.4", {"start": v(148.65, 23.9) * mm, "end": v(145.9, 19.15) * mm});
            skLineSegment(sketch, "E6.7.4.5", {"start": v(147.28, 18.35) * mm, "end": v(150.03, 23.1) * mm});
            skLineSegment(sketch, "E6.7.4.6", {"start": v(150.03, 13.6) * mm, "end": v(147.28, 18.35) * mm});
            skLineSegment(sketch, "E6.7.4.7", {"start": v(155.52, 13.6) * mm, "end": v(150.03, 13.6) * mm});
            skLineSegment(sketch, "E6.7.4.8", {"start": v(158.26, 18.35) * mm, "end": v(155.52, 13.6) * mm});
            skLineSegment(sketch, "E6.7.4.9", {"start": v(155.52, 23.1) * mm, "end": v(158.26, 18.35) * mm});
            skLineSegment(sketch, "E6.7.4.10", {"start": v(150.03, 23.1) * mm, "end": v(155.52, 23.1) * mm});
            skLineSegment(sketch, "E6.7.4.11", {"start": v(140.42, 28.65) * mm, "end": v(145.9, 28.65) * mm});
            skLineSegment(sketch, "E6.7.5.0", {"start": v(145.9, 17.56) * mm, "end": v(148.65, 12.8) * mm});
            skLineSegment(sketch, "E6.7.5.1", {"start": v(137.68, 12.8) * mm, "end": v(140.42, 17.56) * mm});
            skLineSegment(sketch, "E6.7.5.2", {"start": v(140.42, 8.05) * mm, "end": v(137.68, 12.8) * mm});
            skLineSegment(sketch, "E6.7.5.3", {"start": v(145.9, 8.05) * mm, "end": v(140.42, 8.05) * mm});
            skLineSegment(sketch, "E6.7.5.4", {"start": v(148.65, 12.8) * mm, "end": v(145.9, 8.05) * mm});
            skLineSegment(sketch, "E6.7.5.5", {"start": v(147.28, 7.26) * mm, "end": v(150.03, 12.01) * mm});
            skLineSegment(sketch, "E6.7.5.6", {"start": v(150.03, 2.5) * mm, "end": v(147.28, 7.26) * mm});
            skLineSegment(sketch, "E6.7.5.7", {"start": v(155.52, 2.5) * mm, "end": v(150.03, 2.5) * mm});
            skLineSegment(sketch, "E6.7.5.8", {"start": v(158.26, 7.26) * mm, "end": v(155.52, 2.5) * mm});
            skLineSegment(sketch, "E6.7.5.9", {"start": v(155.52, 12.01) * mm, "end": v(158.26, 7.26) * mm});
            skLineSegment(sketch, "E6.7.5.10", {"start": v(150.03, 12.01) * mm, "end": v(155.52, 12.01) * mm});
            skLineSegment(sketch, "E6.7.5.11", {"start": v(140.42, 17.56) * mm, "end": v(145.9, 17.56) * mm});
            skLineSegment(sketch, "E6.8.0.0", {"start": v(165.12, 73.02) * mm, "end": v(167.87, 68.27) * mm});
            skLineSegment(sketch, "E6.8.0.1", {"start": v(156.9, 68.27) * mm, "end": v(159.63, 73.02) * mm});
            skLineSegment(sketch, "E6.8.0.2", {"start": v(159.63, 63.52) * mm, "end": v(156.9, 68.27) * mm});
            skLineSegment(sketch, "E6.8.0.3", {"start": v(165.12, 63.52) * mm, "end": v(159.63, 63.52) * mm});
            skLineSegment(sketch, "E6.8.0.4", {"start": v(167.87, 68.27) * mm, "end": v(165.12, 63.52) * mm});
            skLineSegment(sketch, "E6.8.0.5", {"start": v(166.5, 62.73) * mm, "end": v(169.24, 67.48) * mm});
            skLineSegment(sketch, "E6.8.0.6", {"start": v(169.24, 57.97) * mm, "end": v(166.5, 62.73) * mm});
            skLineSegment(sketch, "E6.8.0.7", {"start": v(174.73, 57.97) * mm, "end": v(169.24, 57.97) * mm});
            skLineSegment(sketch, "E6.8.0.8", {"start": v(177.47, 62.73) * mm, "end": v(174.73, 57.97) * mm});
            skLineSegment(sketch, "E6.8.0.9", {"start": v(174.73, 67.48) * mm, "end": v(177.47, 62.73) * mm});
            skLineSegment(sketch, "E6.8.0.10", {"start": v(169.24, 67.48) * mm, "end": v(174.73, 67.48) * mm});
            skLineSegment(sketch, "E6.8.0.11", {"start": v(159.63, 73.03) * mm, "end": v(165.12, 73.03) * mm});
            skLineSegment(sketch, "E6.8.1.0", {"start": v(165.12, 61.93) * mm, "end": v(167.87, 57.18) * mm});
            skLineSegment(sketch, "E6.8.1.1", {"start": v(156.9, 57.18) * mm, "end": v(159.63, 61.93) * mm});
            skLineSegment(sketch, "E6.8.1.2", {"start": v(159.63, 52.43) * mm, "end": v(156.9, 57.18) * mm});
            skLineSegment(sketch, "E6.8.1.3", {"start": v(165.12, 52.43) * mm, "end": v(159.63, 52.43) * mm});
            skLineSegment(sketch, "E6.8.1.4", {"start": v(167.87, 57.18) * mm, "end": v(165.12, 52.43) * mm});
            skLineSegment(sketch, "E6.8.1.5", {"start": v(166.5, 51.63) * mm, "end": v(169.24, 56.38) * mm});
            skLineSegment(sketch, "E6.8.1.6", {"start": v(169.24, 46.88) * mm, "end": v(166.5, 51.63) * mm});
            skLineSegment(sketch, "E6.8.1.7", {"start": v(174.73, 46.88) * mm, "end": v(169.24, 46.88) * mm});
            skLineSegment(sketch, "E6.8.1.8", {"start": v(177.47, 51.63) * mm, "end": v(174.73, 46.88) * mm});
            skLineSegment(sketch, "E6.8.1.9", {"start": v(174.73, 56.38) * mm, "end": v(177.47, 51.63) * mm});
            skLineSegment(sketch, "E6.8.1.10", {"start": v(169.24, 56.38) * mm, "end": v(174.73, 56.38) * mm});
            skLineSegment(sketch, "E6.8.1.11", {"start": v(159.63, 61.93) * mm, "end": v(165.12, 61.93) * mm});
            skLineSegment(sketch, "E6.8.2.0", {"start": v(165.12, 50.84) * mm, "end": v(167.87, 46.09) * mm});
            skLineSegment(sketch, "E6.8.2.1", {"start": v(156.9, 46.09) * mm, "end": v(159.63, 50.84) * mm});
            skLineSegment(sketch, "E6.8.2.2", {"start": v(159.63, 41.33) * mm, "end": v(156.9, 46.09) * mm});
            skLineSegment(sketch, "E6.8.2.3", {"start": v(165.12, 41.33) * mm, "end": v(159.63, 41.33) * mm});
            skLineSegment(sketch, "E6.8.2.4", {"start": v(167.87, 46.09) * mm, "end": v(165.12, 41.33) * mm});
            skLineSegment(sketch, "E6.8.2.5", {"start": v(166.5, 40.54) * mm, "end": v(169.24, 45.3) * mm});
            skLineSegment(sketch, "E6.8.2.6", {"start": v(169.24, 35.79) * mm, "end": v(166.5, 40.54) * mm});
            skLineSegment(sketch, "E6.8.2.7", {"start": v(174.73, 35.79) * mm, "end": v(169.24, 35.79) * mm});
            skLineSegment(sketch, "E6.8.2.8", {"start": v(177.47, 40.54) * mm, "end": v(174.73, 35.79) * mm});
            skLineSegment(sketch, "E6.8.2.9", {"start": v(174.73, 45.3) * mm, "end": v(177.47, 40.54) * mm});
            skLineSegment(sketch, "E6.8.2.10", {"start": v(169.24, 45.3) * mm, "end": v(174.73, 45.3) * mm});
            skLineSegment(sketch, "E6.8.2.11", {"start": v(159.63, 50.84) * mm, "end": v(165.12, 50.84) * mm});
            skLineSegment(sketch, "E6.8.3.0", {"start": v(165.12, 39.74) * mm, "end": v(167.87, 35) * mm});
            skLineSegment(sketch, "E6.8.3.1", {"start": v(156.9, 35) * mm, "end": v(159.63, 39.74) * mm});
            skLineSegment(sketch, "E6.8.3.2", {"start": v(159.63, 30.24) * mm, "end": v(156.9, 35) * mm});
            skLineSegment(sketch, "E6.8.3.3", {"start": v(165.12, 30.24) * mm, "end": v(159.63, 30.24) * mm});
            skLineSegment(sketch, "E6.8.3.4", {"start": v(167.87, 35) * mm, "end": v(165.12, 30.24) * mm});
            skLineSegment(sketch, "E6.8.3.5", {"start": v(166.5, 29.44) * mm, "end": v(169.24, 34.2) * mm});
            skLineSegment(sketch, "E6.8.3.6", {"start": v(169.24, 24.7) * mm, "end": v(166.5, 29.44) * mm});
            skLineSegment(sketch, "E6.8.3.7", {"start": v(174.73, 24.7) * mm, "end": v(169.24, 24.7) * mm});
            skLineSegment(sketch, "E6.8.3.8", {"start": v(177.47, 29.44) * mm, "end": v(174.73, 24.7) * mm});
            skLineSegment(sketch, "E6.8.3.9", {"start": v(174.73, 34.2) * mm, "end": v(177.47, 29.44) * mm});
            skLineSegment(sketch, "E6.8.3.10", {"start": v(169.24, 34.2) * mm, "end": v(174.73, 34.2) * mm});
            skLineSegment(sketch, "E6.8.3.11", {"start": v(159.63, 39.74) * mm, "end": v(165.12, 39.74) * mm});
            skLineSegment(sketch, "E6.8.4.0", {"start": v(165.12, 28.65) * mm, "end": v(167.87, 23.9) * mm});
            skLineSegment(sketch, "E6.8.4.1", {"start": v(156.9, 23.9) * mm, "end": v(159.63, 28.65) * mm});
            skLineSegment(sketch, "E6.8.4.2", {"start": v(159.63, 19.15) * mm, "end": v(156.9, 23.9) * mm});
            skLineSegment(sketch, "E6.8.4.3", {"start": v(165.12, 19.15) * mm, "end": v(159.63, 19.15) * mm});
            skLineSegment(sketch, "E6.8.4.4", {"start": v(167.87, 23.9) * mm, "end": v(165.12, 19.15) * mm});
            skLineSegment(sketch, "E6.8.4.5", {"start": v(166.5, 18.35) * mm, "end": v(169.24, 23.1) * mm});
            skLineSegment(sketch, "E6.8.4.6", {"start": v(169.24, 13.6) * mm, "end": v(166.5, 18.35) * mm});
            skLineSegment(sketch, "E6.8.4.7", {"start": v(174.73, 13.6) * mm, "end": v(169.24, 13.6) * mm});
            skLineSegment(sketch, "E6.8.4.8", {"start": v(177.47, 18.35) * mm, "end": v(174.73, 13.6) * mm});
            skLineSegment(sketch, "E6.8.4.9", {"start": v(174.73, 23.1) * mm, "end": v(177.47, 18.35) * mm});
            skLineSegment(sketch, "E6.8.4.10", {"start": v(169.24, 23.1) * mm, "end": v(174.73, 23.1) * mm});
            skLineSegment(sketch, "E6.8.4.11", {"start": v(159.63, 28.65) * mm, "end": v(165.12, 28.65) * mm});
            skLineSegment(sketch, "E6.8.5.0", {"start": v(165.12, 17.56) * mm, "end": v(167.87, 12.8) * mm});
            skLineSegment(sketch, "E6.8.5.1", {"start": v(156.9, 12.8) * mm, "end": v(159.63, 17.56) * mm});
            skLineSegment(sketch, "E6.8.5.2", {"start": v(159.63, 8.05) * mm, "end": v(156.9, 12.8) * mm});
            skLineSegment(sketch, "E6.8.5.3", {"start": v(165.12, 8.05) * mm, "end": v(159.63, 8.05) * mm});
            skLineSegment(sketch, "E6.8.5.4", {"start": v(167.87, 12.8) * mm, "end": v(165.12, 8.05) * mm});
            skLineSegment(sketch, "E6.8.5.5", {"start": v(166.5, 7.26) * mm, "end": v(169.24, 12.01) * mm});
            skLineSegment(sketch, "E6.8.5.6", {"start": v(169.24, 2.5) * mm, "end": v(166.5, 7.26) * mm});
            skLineSegment(sketch, "E6.8.5.7", {"start": v(174.73, 2.5) * mm, "end": v(169.24, 2.5) * mm});
            skLineSegment(sketch, "E6.8.5.8", {"start": v(177.47, 7.26) * mm, "end": v(174.73, 2.5) * mm});
            skLineSegment(sketch, "E6.8.5.9", {"start": v(174.73, 12.01) * mm, "end": v(177.47, 7.26) * mm});
            skLineSegment(sketch, "E6.8.5.10", {"start": v(169.24, 12.01) * mm, "end": v(174.73, 12.01) * mm});
            skLineSegment(sketch, "E6.8.5.11", {"start": v(159.63, 17.56) * mm, "end": v(165.12, 17.56) * mm});
            skLineSegment(sketch, "E6.9.0.0", {"start": v(184.34, 73.02) * mm, "end": v(187.08, 68.27) * mm});
            skLineSegment(sketch, "E6.9.0.1", {"start": v(176.1, 68.27) * mm, "end": v(178.85, 73.02) * mm});
            skLineSegment(sketch, "E6.9.0.2", {"start": v(178.85, 63.52) * mm, "end": v(176.1, 68.27) * mm});
            skLineSegment(sketch, "E6.9.0.3", {"start": v(184.34, 63.52) * mm, "end": v(178.85, 63.52) * mm});
            skLineSegment(sketch, "E6.9.0.4", {"start": v(187.08, 68.27) * mm, "end": v(184.34, 63.52) * mm});
            skLineSegment(sketch, "E6.9.0.5", {"start": v(185.71, 62.73) * mm, "end": v(188.46, 67.48) * mm});
            skLineSegment(sketch, "E6.9.0.6", {"start": v(188.46, 57.97) * mm, "end": v(185.71, 62.73) * mm});
            skLineSegment(sketch, "E6.9.0.7", {"start": v(193.94, 57.97) * mm, "end": v(188.46, 57.97) * mm});
            skLineSegment(sketch, "E6.9.0.8", {"start": v(196.69, 62.73) * mm, "end": v(193.94, 57.97) * mm});
            skLineSegment(sketch, "E6.9.0.9", {"start": v(193.94, 67.48) * mm, "end": v(196.69, 62.73) * mm});
            skLineSegment(sketch, "E6.9.0.10", {"start": v(188.46, 67.48) * mm, "end": v(193.94, 67.48) * mm});
            skLineSegment(sketch, "E6.9.0.11", {"start": v(178.85, 73.03) * mm, "end": v(184.34, 73.03) * mm});
            skLineSegment(sketch, "E6.9.1.0", {"start": v(184.34, 61.93) * mm, "end": v(187.08, 57.18) * mm});
            skLineSegment(sketch, "E6.9.1.1", {"start": v(176.1, 57.18) * mm, "end": v(178.85, 61.93) * mm});
            skLineSegment(sketch, "E6.9.1.2", {"start": v(178.85, 52.43) * mm, "end": v(176.1, 57.18) * mm});
            skLineSegment(sketch, "E6.9.1.3", {"start": v(184.34, 52.43) * mm, "end": v(178.85, 52.43) * mm});
            skLineSegment(sketch, "E6.9.1.4", {"start": v(187.08, 57.18) * mm, "end": v(184.34, 52.43) * mm});
            skLineSegment(sketch, "E6.9.1.5", {"start": v(185.71, 51.63) * mm, "end": v(188.46, 56.38) * mm});
            skLineSegment(sketch, "E6.9.1.6", {"start": v(188.46, 46.88) * mm, "end": v(185.71, 51.63) * mm});
            skLineSegment(sketch, "E6.9.1.7", {"start": v(193.94, 46.88) * mm, "end": v(188.46, 46.88) * mm});
            skLineSegment(sketch, "E6.9.1.8", {"start": v(196.69, 51.63) * mm, "end": v(193.94, 46.88) * mm});
            skLineSegment(sketch, "E6.9.1.9", {"start": v(193.94, 56.38) * mm, "end": v(196.69, 51.63) * mm});
            skLineSegment(sketch, "E6.9.1.10", {"start": v(188.46, 56.38) * mm, "end": v(193.94, 56.38) * mm});
            skLineSegment(sketch, "E6.9.1.11", {"start": v(178.85, 61.93) * mm, "end": v(184.34, 61.93) * mm});
            skLineSegment(sketch, "E6.9.2.0", {"start": v(184.34, 50.84) * mm, "end": v(187.08, 46.09) * mm});
            skLineSegment(sketch, "E6.9.2.1", {"start": v(176.1, 46.09) * mm, "end": v(178.85, 50.84) * mm});
            skLineSegment(sketch, "E6.9.2.2", {"start": v(178.85, 41.33) * mm, "end": v(176.1, 46.09) * mm});
            skLineSegment(sketch, "E6.9.2.3", {"start": v(184.34, 41.33) * mm, "end": v(178.85, 41.33) * mm});
            skLineSegment(sketch, "E6.9.2.4", {"start": v(187.08, 46.09) * mm, "end": v(184.34, 41.33) * mm});
            skLineSegment(sketch, "E6.9.2.5", {"start": v(185.71, 40.54) * mm, "end": v(188.46, 45.3) * mm});
            skLineSegment(sketch, "E6.9.2.6", {"start": v(188.46, 35.79) * mm, "end": v(185.71, 40.54) * mm});
            skLineSegment(sketch, "E6.9.2.7", {"start": v(193.94, 35.79) * mm, "end": v(188.46, 35.79) * mm});
            skLineSegment(sketch, "E6.9.2.8", {"start": v(196.69, 40.54) * mm, "end": v(193.94, 35.79) * mm});
            skLineSegment(sketch, "E6.9.2.9", {"start": v(193.94, 45.3) * mm, "end": v(196.69, 40.54) * mm});
            skLineSegment(sketch, "E6.9.2.10", {"start": v(188.46, 45.3) * mm, "end": v(193.94, 45.3) * mm});
            skLineSegment(sketch, "E6.9.2.11", {"start": v(178.85, 50.84) * mm, "end": v(184.34, 50.84) * mm});
            skLineSegment(sketch, "E6.9.3.0", {"start": v(184.34, 39.74) * mm, "end": v(187.08, 35) * mm});
            skLineSegment(sketch, "E6.9.3.1", {"start": v(176.1, 35) * mm, "end": v(178.85, 39.74) * mm});
            skLineSegment(sketch, "E6.9.3.2", {"start": v(178.85, 30.24) * mm, "end": v(176.1, 35) * mm});
            skLineSegment(sketch, "E6.9.3.3", {"start": v(184.34, 30.24) * mm, "end": v(178.85, 30.24) * mm});
            skLineSegment(sketch, "E6.9.3.4", {"start": v(187.08, 35) * mm, "end": v(184.34, 30.24) * mm});
            skLineSegment(sketch, "E6.9.3.5", {"start": v(185.71, 29.44) * mm, "end": v(188.46, 34.2) * mm});
            skLineSegment(sketch, "E6.9.3.6", {"start": v(188.46, 24.7) * mm, "end": v(185.71, 29.44) * mm});
            skLineSegment(sketch, "E6.9.3.7", {"start": v(193.94, 24.7) * mm, "end": v(188.46, 24.7) * mm});
            skLineSegment(sketch, "E6.9.3.8", {"start": v(196.69, 29.44) * mm, "end": v(193.94, 24.7) * mm});
            skLineSegment(sketch, "E6.9.3.9", {"start": v(193.94, 34.2) * mm, "end": v(196.69, 29.44) * mm});
            skLineSegment(sketch, "E6.9.3.10", {"start": v(188.46, 34.2) * mm, "end": v(193.94, 34.2) * mm});
            skLineSegment(sketch, "E6.9.3.11", {"start": v(178.85, 39.74) * mm, "end": v(184.34, 39.74) * mm});
            skLineSegment(sketch, "E6.9.4.0", {"start": v(184.34, 28.65) * mm, "end": v(187.08, 23.9) * mm});
            skLineSegment(sketch, "E6.9.4.1", {"start": v(176.1, 23.9) * mm, "end": v(178.85, 28.65) * mm});
            skLineSegment(sketch, "E6.9.4.2", {"start": v(178.85, 19.15) * mm, "end": v(176.1, 23.9) * mm});
            skLineSegment(sketch, "E6.9.4.3", {"start": v(184.34, 19.15) * mm, "end": v(178.85, 19.15) * mm});
            skLineSegment(sketch, "E6.9.4.4", {"start": v(187.08, 23.9) * mm, "end": v(184.34, 19.15) * mm});
            skLineSegment(sketch, "E6.9.4.5", {"start": v(185.71, 18.35) * mm, "end": v(188.46, 23.1) * mm});
            skLineSegment(sketch, "E6.9.4.6", {"start": v(188.46, 13.6) * mm, "end": v(185.71, 18.35) * mm});
            skLineSegment(sketch, "E6.9.4.7", {"start": v(193.94, 13.6) * mm, "end": v(188.46, 13.6) * mm});
            skLineSegment(sketch, "E6.9.4.8", {"start": v(196.69, 18.35) * mm, "end": v(193.94, 13.6) * mm});
            skLineSegment(sketch, "E6.9.4.9", {"start": v(193.94, 23.1) * mm, "end": v(196.69, 18.35) * mm});
            skLineSegment(sketch, "E6.9.4.10", {"start": v(188.46, 23.1) * mm, "end": v(193.94, 23.1) * mm});
            skLineSegment(sketch, "E6.9.4.11", {"start": v(178.85, 28.65) * mm, "end": v(184.34, 28.65) * mm});
            skLineSegment(sketch, "E6.9.5.0", {"start": v(184.34, 17.56) * mm, "end": v(187.08, 12.8) * mm});
            skLineSegment(sketch, "E6.9.5.1", {"start": v(176.1, 12.8) * mm, "end": v(178.85, 17.56) * mm});
            skLineSegment(sketch, "E6.9.5.2", {"start": v(178.85, 8.05) * mm, "end": v(176.1, 12.8) * mm});
            skLineSegment(sketch, "E6.9.5.3", {"start": v(184.34, 8.05) * mm, "end": v(178.85, 8.05) * mm});
            skLineSegment(sketch, "E6.9.5.4", {"start": v(187.08, 12.8) * mm, "end": v(184.34, 8.05) * mm});
            skLineSegment(sketch, "E6.9.5.5", {"start": v(185.71, 7.26) * mm, "end": v(188.46, 12.01) * mm});
            skLineSegment(sketch, "E6.9.5.6", {"start": v(188.46, 2.5) * mm, "end": v(185.71, 7.26) * mm});
            skLineSegment(sketch, "E6.9.5.7", {"start": v(193.94, 2.5) * mm, "end": v(188.46, 2.5) * mm});
            skLineSegment(sketch, "E6.9.5.8", {"start": v(196.69, 7.26) * mm, "end": v(193.94, 2.5) * mm});
            skLineSegment(sketch, "E6.9.5.9", {"start": v(193.94, 12.01) * mm, "end": v(196.69, 7.26) * mm});
            skLineSegment(sketch, "E6.9.5.10", {"start": v(188.46, 12.01) * mm, "end": v(193.94, 12.01) * mm});
            skLineSegment(sketch, "E6.9.5.11", {"start": v(178.85, 17.56) * mm, "end": v(184.34, 17.56) * mm});
            skLineSegment(sketch, "E6.10.0.0", {"start": v(203.55, 73.02) * mm, "end": v(206.3, 68.27) * mm});
            skLineSegment(sketch, "E6.10.0.1", {"start": v(195.32, 68.27) * mm, "end": v(198.06, 73.02) * mm});
            skLineSegment(sketch, "E6.10.0.2", {"start": v(198.06, 63.52) * mm, "end": v(195.32, 68.27) * mm});
            skLineSegment(sketch, "E6.10.0.3", {"start": v(203.55, 63.52) * mm, "end": v(198.06, 63.52) * mm});
            skLineSegment(sketch, "E6.10.0.4", {"start": v(206.3, 68.27) * mm, "end": v(203.55, 63.52) * mm});
            skLineSegment(sketch, "E6.10.0.5", {"start": v(204.93, 62.73) * mm, "end": v(207.67, 67.48) * mm});
            skLineSegment(sketch, "E6.10.0.6", {"start": v(207.67, 57.97) * mm, "end": v(204.93, 62.73) * mm});
            skLineSegment(sketch, "E6.10.0.7", {"start": v(213.16, 57.97) * mm, "end": v(207.67, 57.97) * mm});
            skLineSegment(sketch, "E6.10.0.8", {"start": v(215.9, 62.73) * mm, "end": v(213.16, 57.97) * mm});
            skLineSegment(sketch, "E6.10.0.9", {"start": v(213.16, 67.48) * mm, "end": v(215.9, 62.73) * mm});
            skLineSegment(sketch, "E6.10.0.10", {"start": v(207.67, 67.48) * mm, "end": v(213.16, 67.48) * mm});
            skLineSegment(sketch, "E6.10.0.11", {"start": v(198.06, 73.03) * mm, "end": v(203.55, 73.03) * mm});
            skLineSegment(sketch, "E6.10.1.0", {"start": v(203.55, 61.93) * mm, "end": v(206.3, 57.18) * mm});
            skLineSegment(sketch, "E6.10.1.1", {"start": v(195.32, 57.18) * mm, "end": v(198.06, 61.93) * mm});
            skLineSegment(sketch, "E6.10.1.2", {"start": v(198.06, 52.43) * mm, "end": v(195.32, 57.18) * mm});
            skLineSegment(sketch, "E6.10.1.3", {"start": v(203.55, 52.43) * mm, "end": v(198.06, 52.43) * mm});
            skLineSegment(sketch, "E6.10.1.4", {"start": v(206.3, 57.18) * mm, "end": v(203.55, 52.43) * mm});
            skLineSegment(sketch, "E6.10.1.5", {"start": v(204.93, 51.63) * mm, "end": v(207.67, 56.38) * mm});
            skLineSegment(sketch, "E6.10.1.6", {"start": v(207.67, 46.88) * mm, "end": v(204.93, 51.63) * mm});
            skLineSegment(sketch, "E6.10.1.7", {"start": v(213.16, 46.88) * mm, "end": v(207.67, 46.88) * mm});
            skLineSegment(sketch, "E6.10.1.8", {"start": v(215.9, 51.63) * mm, "end": v(213.16, 46.88) * mm});
            skLineSegment(sketch, "E6.10.1.9", {"start": v(213.16, 56.38) * mm, "end": v(215.9, 51.63) * mm});
            skLineSegment(sketch, "E6.10.1.10", {"start": v(207.67, 56.38) * mm, "end": v(213.16, 56.38) * mm});
            skLineSegment(sketch, "E6.10.1.11", {"start": v(198.06, 61.93) * mm, "end": v(203.55, 61.93) * mm});
            skLineSegment(sketch, "E6.10.2.0", {"start": v(203.55, 50.84) * mm, "end": v(206.3, 46.09) * mm});
            skLineSegment(sketch, "E6.10.2.1", {"start": v(195.32, 46.09) * mm, "end": v(198.06, 50.84) * mm});
            skLineSegment(sketch, "E6.10.2.2", {"start": v(198.06, 41.33) * mm, "end": v(195.32, 46.09) * mm});
            skLineSegment(sketch, "E6.10.2.3", {"start": v(203.55, 41.33) * mm, "end": v(198.06, 41.33) * mm});
            skLineSegment(sketch, "E6.10.2.4", {"start": v(206.3, 46.09) * mm, "end": v(203.55, 41.33) * mm});
            skLineSegment(sketch, "E6.10.2.5", {"start": v(204.93, 40.54) * mm, "end": v(207.67, 45.3) * mm});
            skLineSegment(sketch, "E6.10.2.6", {"start": v(207.67, 35.79) * mm, "end": v(204.93, 40.54) * mm});
            skLineSegment(sketch, "E6.10.2.7", {"start": v(213.16, 35.79) * mm, "end": v(207.67, 35.79) * mm});
            skLineSegment(sketch, "E6.10.2.8", {"start": v(215.9, 40.54) * mm, "end": v(213.16, 35.79) * mm});
            skLineSegment(sketch, "E6.10.2.9", {"start": v(213.16, 45.3) * mm, "end": v(215.9, 40.54) * mm});
            skLineSegment(sketch, "E6.10.2.10", {"start": v(207.67, 45.3) * mm, "end": v(213.16, 45.3) * mm});
            skLineSegment(sketch, "E6.10.2.11", {"start": v(198.06, 50.84) * mm, "end": v(203.55, 50.84) * mm});
            skLineSegment(sketch, "E6.10.3.0", {"start": v(203.55, 39.74) * mm, "end": v(206.3, 35) * mm});
            skLineSegment(sketch, "E6.10.3.1", {"start": v(195.32, 35) * mm, "end": v(198.06, 39.74) * mm});
            skLineSegment(sketch, "E6.10.3.2", {"start": v(198.06, 30.24) * mm, "end": v(195.32, 35) * mm});
            skLineSegment(sketch, "E6.10.3.3", {"start": v(203.55, 30.24) * mm, "end": v(198.06, 30.24) * mm});
            skLineSegment(sketch, "E6.10.3.4", {"start": v(206.3, 35) * mm, "end": v(203.55, 30.24) * mm});
            skLineSegment(sketch, "E6.10.3.5", {"start": v(204.93, 29.44) * mm, "end": v(207.67, 34.2) * mm});
            skLineSegment(sketch, "E6.10.3.6", {"start": v(207.67, 24.7) * mm, "end": v(204.93, 29.44) * mm});
            skLineSegment(sketch, "E6.10.3.7", {"start": v(213.16, 24.7) * mm, "end": v(207.67, 24.7) * mm});
            skLineSegment(sketch, "E6.10.3.8", {"start": v(215.9, 29.44) * mm, "end": v(213.16, 24.7) * mm});
            skLineSegment(sketch, "E6.10.3.9", {"start": v(213.16, 34.2) * mm, "end": v(215.9, 29.44) * mm});
            skLineSegment(sketch, "E6.10.3.10", {"start": v(207.67, 34.2) * mm, "end": v(213.16, 34.2) * mm});
            skLineSegment(sketch, "E6.10.3.11", {"start": v(198.06, 39.74) * mm, "end": v(203.55, 39.74) * mm});
            skLineSegment(sketch, "E6.10.4.0", {"start": v(203.55, 28.65) * mm, "end": v(206.3, 23.9) * mm});
            skLineSegment(sketch, "E6.10.4.1", {"start": v(195.32, 23.9) * mm, "end": v(198.06, 28.65) * mm});
            skLineSegment(sketch, "E6.10.4.2", {"start": v(198.06, 19.15) * mm, "end": v(195.32, 23.9) * mm});
            skLineSegment(sketch, "E6.10.4.3", {"start": v(203.55, 19.15) * mm, "end": v(198.06, 19.15) * mm});
            skLineSegment(sketch, "E6.10.4.4", {"start": v(206.3, 23.9) * mm, "end": v(203.55, 19.15) * mm});
            skLineSegment(sketch, "E6.10.4.5", {"start": v(204.93, 18.35) * mm, "end": v(207.67, 23.1) * mm});
            skLineSegment(sketch, "E6.10.4.6", {"start": v(207.67, 13.6) * mm, "end": v(204.93, 18.35) * mm});
            skLineSegment(sketch, "E6.10.4.7", {"start": v(213.16, 13.6) * mm, "end": v(207.67, 13.6) * mm});
            skLineSegment(sketch, "E6.10.4.8", {"start": v(215.9, 18.35) * mm, "end": v(213.16, 13.6) * mm});
            skLineSegment(sketch, "E6.10.4.9", {"start": v(213.16, 23.1) * mm, "end": v(215.9, 18.35) * mm});
            skLineSegment(sketch, "E6.10.4.10", {"start": v(207.67, 23.1) * mm, "end": v(213.16, 23.1) * mm});
            skLineSegment(sketch, "E6.10.4.11", {"start": v(198.06, 28.65) * mm, "end": v(203.55, 28.65) * mm});
            skLineSegment(sketch, "E6.10.5.0", {"start": v(203.55, 17.56) * mm, "end": v(206.3, 12.8) * mm});
            skLineSegment(sketch, "E6.10.5.1", {"start": v(195.32, 12.8) * mm, "end": v(198.06, 17.56) * mm});
            skLineSegment(sketch, "E6.10.5.2", {"start": v(198.06, 8.05) * mm, "end": v(195.32, 12.8) * mm});
            skLineSegment(sketch, "E6.10.5.3", {"start": v(203.55, 8.05) * mm, "end": v(198.06, 8.05) * mm});
            skLineSegment(sketch, "E6.10.5.4", {"start": v(206.3, 12.8) * mm, "end": v(203.55, 8.05) * mm});
            skLineSegment(sketch, "E6.10.5.5", {"start": v(204.93, 7.26) * mm, "end": v(207.67, 12.01) * mm});
            skLineSegment(sketch, "E6.10.5.6", {"start": v(207.67, 2.5) * mm, "end": v(204.93, 7.26) * mm});
            skLineSegment(sketch, "E6.10.5.7", {"start": v(213.16, 2.5) * mm, "end": v(207.67, 2.5) * mm});
            skLineSegment(sketch, "E6.10.5.8", {"start": v(215.9, 7.26) * mm, "end": v(213.16, 2.5) * mm});
            skLineSegment(sketch, "E6.10.5.9", {"start": v(213.16, 12.01) * mm, "end": v(215.9, 7.26) * mm});
            skLineSegment(sketch, "E6.10.5.10", {"start": v(207.67, 12.01) * mm, "end": v(213.16, 12.01) * mm});
            skLineSegment(sketch, "E6.10.5.11", {"start": v(198.06, 17.56) * mm, "end": v(203.55, 17.56) * mm});
            skLineSegment(sketch, "E6.11.0.0", {"start": v(222.77, 73.02) * mm, "end": v(225.51, 68.27) * mm});
            skLineSegment(sketch, "E6.11.0.1", {"start": v(214.53, 68.27) * mm, "end": v(217.28, 73.02) * mm});
            skLineSegment(sketch, "E6.11.0.2", {"start": v(217.28, 63.52) * mm, "end": v(214.53, 68.27) * mm});
            skLineSegment(sketch, "E6.11.0.3", {"start": v(222.77, 63.52) * mm, "end": v(217.28, 63.52) * mm});
            skLineSegment(sketch, "E6.11.0.4", {"start": v(225.51, 68.27) * mm, "end": v(222.77, 63.52) * mm});
            skLineSegment(sketch, "E6.11.0.5", {"start": v(224.14, 62.73) * mm, "end": v(226.89, 67.48) * mm});
            skLineSegment(sketch, "E6.11.0.6", {"start": v(226.89, 57.97) * mm, "end": v(224.14, 62.73) * mm});
            skLineSegment(sketch, "E6.11.0.7", {"start": v(232.37, 57.97) * mm, "end": v(226.89, 57.97) * mm});
            skLineSegment(sketch, "E6.11.0.8", {"start": v(235.12, 62.73) * mm, "end": v(232.37, 57.97) * mm});
            skLineSegment(sketch, "E6.11.0.9", {"start": v(232.37, 67.48) * mm, "end": v(235.12, 62.73) * mm});
            skLineSegment(sketch, "E6.11.0.10", {"start": v(226.89, 67.48) * mm, "end": v(232.37, 67.48) * mm});
            skLineSegment(sketch, "E6.11.0.11", {"start": v(217.28, 73.03) * mm, "end": v(222.77, 73.03) * mm});
            skLineSegment(sketch, "E6.11.1.0", {"start": v(222.77, 61.93) * mm, "end": v(225.51, 57.18) * mm});
            skLineSegment(sketch, "E6.11.1.1", {"start": v(214.53, 57.18) * mm, "end": v(217.28, 61.93) * mm});
            skLineSegment(sketch, "E6.11.1.2", {"start": v(217.28, 52.43) * mm, "end": v(214.53, 57.18) * mm});
            skLineSegment(sketch, "E6.11.1.3", {"start": v(222.77, 52.43) * mm, "end": v(217.28, 52.43) * mm});
            skLineSegment(sketch, "E6.11.1.4", {"start": v(225.51, 57.18) * mm, "end": v(222.77, 52.43) * mm});
            skLineSegment(sketch, "E6.11.1.5", {"start": v(224.14, 51.63) * mm, "end": v(226.89, 56.38) * mm});
            skLineSegment(sketch, "E6.11.1.6", {"start": v(226.89, 46.88) * mm, "end": v(224.14, 51.63) * mm});
            skLineSegment(sketch, "E6.11.1.7", {"start": v(232.37, 46.88) * mm, "end": v(226.89, 46.88) * mm});
            skLineSegment(sketch, "E6.11.1.8", {"start": v(235.12, 51.63) * mm, "end": v(232.37, 46.88) * mm});
            skLineSegment(sketch, "E6.11.1.9", {"start": v(232.37, 56.38) * mm, "end": v(235.12, 51.63) * mm});
            skLineSegment(sketch, "E6.11.1.10", {"start": v(226.89, 56.38) * mm, "end": v(232.37, 56.38) * mm});
            skLineSegment(sketch, "E6.11.1.11", {"start": v(217.28, 61.93) * mm, "end": v(222.77, 61.93) * mm});
            skLineSegment(sketch, "E6.11.2.0", {"start": v(222.77, 50.84) * mm, "end": v(225.51, 46.09) * mm});
            skLineSegment(sketch, "E6.11.2.1", {"start": v(214.53, 46.09) * mm, "end": v(217.28, 50.84) * mm});
            skLineSegment(sketch, "E6.11.2.2", {"start": v(217.28, 41.33) * mm, "end": v(214.53, 46.09) * mm});
            skLineSegment(sketch, "E6.11.2.3", {"start": v(222.77, 41.33) * mm, "end": v(217.28, 41.33) * mm});
            skLineSegment(sketch, "E6.11.2.4", {"start": v(225.51, 46.09) * mm, "end": v(222.77, 41.33) * mm});
            skLineSegment(sketch, "E6.11.2.5", {"start": v(224.14, 40.54) * mm, "end": v(226.89, 45.3) * mm});
            skLineSegment(sketch, "E6.11.2.6", {"start": v(226.89, 35.79) * mm, "end": v(224.14, 40.54) * mm});
            skLineSegment(sketch, "E6.11.2.7", {"start": v(232.37, 35.79) * mm, "end": v(226.89, 35.79) * mm});
            skLineSegment(sketch, "E6.11.2.8", {"start": v(235.12, 40.54) * mm, "end": v(232.37, 35.79) * mm});
            skLineSegment(sketch, "E6.11.2.9", {"start": v(232.37, 45.3) * mm, "end": v(235.12, 40.54) * mm});
            skLineSegment(sketch, "E6.11.2.10", {"start": v(226.89, 45.3) * mm, "end": v(232.37, 45.3) * mm});
            skLineSegment(sketch, "E6.11.2.11", {"start": v(217.28, 50.84) * mm, "end": v(222.77, 50.84) * mm});
            skLineSegment(sketch, "E6.11.3.0", {"start": v(222.77, 39.74) * mm, "end": v(225.51, 35) * mm});
            skLineSegment(sketch, "E6.11.3.1", {"start": v(214.53, 35) * mm, "end": v(217.28, 39.74) * mm});
            skLineSegment(sketch, "E6.11.3.2", {"start": v(217.28, 30.24) * mm, "end": v(214.53, 35) * mm});
            skLineSegment(sketch, "E6.11.3.3", {"start": v(222.77, 30.24) * mm, "end": v(217.28, 30.24) * mm});
            skLineSegment(sketch, "E6.11.3.4", {"start": v(225.51, 35) * mm, "end": v(222.77, 30.24) * mm});
            skLineSegment(sketch, "E6.11.3.5", {"start": v(224.14, 29.44) * mm, "end": v(226.89, 34.2) * mm});
            skLineSegment(sketch, "E6.11.3.6", {"start": v(226.89, 24.7) * mm, "end": v(224.14, 29.44) * mm});
            skLineSegment(sketch, "E6.11.3.7", {"start": v(232.37, 24.7) * mm, "end": v(226.89, 24.7) * mm});
            skLineSegment(sketch, "E6.11.3.8", {"start": v(235.12, 29.44) * mm, "end": v(232.37, 24.7) * mm});
            skLineSegment(sketch, "E6.11.3.9", {"start": v(232.37, 34.2) * mm, "end": v(235.12, 29.44) * mm});
            skLineSegment(sketch, "E6.11.3.10", {"start": v(226.89, 34.2) * mm, "end": v(232.37, 34.2) * mm});
            skLineSegment(sketch, "E6.11.3.11", {"start": v(217.28, 39.74) * mm, "end": v(222.77, 39.74) * mm});
            skLineSegment(sketch, "E6.11.4.0", {"start": v(222.77, 28.65) * mm, "end": v(225.51, 23.9) * mm});
            skLineSegment(sketch, "E6.11.4.1", {"start": v(214.53, 23.9) * mm, "end": v(217.28, 28.65) * mm});
            skLineSegment(sketch, "E6.11.4.2", {"start": v(217.28, 19.15) * mm, "end": v(214.53, 23.9) * mm});
            skLineSegment(sketch, "E6.11.4.3", {"start": v(222.77, 19.15) * mm, "end": v(217.28, 19.15) * mm});
            skLineSegment(sketch, "E6.11.4.4", {"start": v(225.51, 23.9) * mm, "end": v(222.77, 19.15) * mm});
            skLineSegment(sketch, "E6.11.4.5", {"start": v(224.14, 18.35) * mm, "end": v(226.89, 23.1) * mm});
            skLineSegment(sketch, "E6.11.4.6", {"start": v(226.89, 13.6) * mm, "end": v(224.14, 18.35) * mm});
            skLineSegment(sketch, "E6.11.4.7", {"start": v(232.37, 13.6) * mm, "end": v(226.89, 13.6) * mm});
            skLineSegment(sketch, "E6.11.4.8", {"start": v(235.12, 18.35) * mm, "end": v(232.37, 13.6) * mm});
            skLineSegment(sketch, "E6.11.4.9", {"start": v(232.37, 23.1) * mm, "end": v(235.12, 18.35) * mm});
            skLineSegment(sketch, "E6.11.4.10", {"start": v(226.89, 23.1) * mm, "end": v(232.37, 23.1) * mm});
            skLineSegment(sketch, "E6.11.4.11", {"start": v(217.28, 28.65) * mm, "end": v(222.77, 28.65) * mm});
            skLineSegment(sketch, "E6.11.5.0", {"start": v(222.77, 17.56) * mm, "end": v(225.51, 12.8) * mm});
            skLineSegment(sketch, "E6.11.5.1", {"start": v(214.53, 12.8) * mm, "end": v(217.28, 17.56) * mm});
            skLineSegment(sketch, "E6.11.5.2", {"start": v(217.28, 8.05) * mm, "end": v(214.53, 12.8) * mm});
            skLineSegment(sketch, "E6.11.5.3", {"start": v(222.77, 8.05) * mm, "end": v(217.28, 8.05) * mm});
            skLineSegment(sketch, "E6.11.5.4", {"start": v(225.51, 12.8) * mm, "end": v(222.77, 8.05) * mm});
            skLineSegment(sketch, "E6.11.5.5", {"start": v(224.14, 7.26) * mm, "end": v(226.89, 12.01) * mm});
            skLineSegment(sketch, "E6.11.5.6", {"start": v(226.89, 2.5) * mm, "end": v(224.14, 7.26) * mm});
            skLineSegment(sketch, "E6.11.5.7", {"start": v(232.37, 2.5) * mm, "end": v(226.89, 2.5) * mm});
            skLineSegment(sketch, "E6.11.5.8", {"start": v(235.12, 7.26) * mm, "end": v(232.37, 2.5) * mm});
            skLineSegment(sketch, "E6.11.5.9", {"start": v(232.37, 12.01) * mm, "end": v(235.12, 7.26) * mm});
            skLineSegment(sketch, "E6.11.5.10", {"start": v(226.89, 12.01) * mm, "end": v(232.37, 12.01) * mm});
            skLineSegment(sketch, "E6.11.5.11", {"start": v(217.28, 17.56) * mm, "end": v(222.77, 17.56) * mm});
            skLineSegment(sketch, "E6.12.0.0", {"start": v(241.98, 73.02) * mm, "end": v(244.72, 68.27) * mm});
            skLineSegment(sketch, "E6.12.0.1", {"start": v(233.75, 68.27) * mm, "end": v(236.5, 73.02) * mm});
            skLineSegment(sketch, "E6.12.0.2", {"start": v(236.5, 63.52) * mm, "end": v(233.75, 68.27) * mm});
            skLineSegment(sketch, "E6.12.0.3", {"start": v(241.98, 63.52) * mm, "end": v(236.5, 63.52) * mm});
            skLineSegment(sketch, "E6.12.0.4", {"start": v(244.72, 68.27) * mm, "end": v(241.98, 63.52) * mm});
            skLineSegment(sketch, "E6.12.0.5", {"start": v(243.36, 62.73) * mm, "end": v(246.1, 67.48) * mm});
            skLineSegment(sketch, "E6.12.0.6", {"start": v(246.1, 57.97) * mm, "end": v(243.36, 62.73) * mm});
            skLineSegment(sketch, "E6.12.0.7", {"start": v(251.59, 57.97) * mm, "end": v(246.1, 57.97) * mm});
            skLineSegment(sketch, "E6.12.0.8", {"start": v(254.33, 62.73) * mm, "end": v(251.59, 57.97) * mm});
            skLineSegment(sketch, "E6.12.0.9", {"start": v(251.59, 67.48) * mm, "end": v(254.33, 62.73) * mm});
            skLineSegment(sketch, "E6.12.0.10", {"start": v(246.1, 67.48) * mm, "end": v(251.59, 67.48) * mm});
            skLineSegment(sketch, "E6.12.0.11", {"start": v(236.5, 73.03) * mm, "end": v(241.98, 73.03) * mm});
            skLineSegment(sketch, "E6.12.1.0", {"start": v(241.98, 61.93) * mm, "end": v(244.72, 57.18) * mm});
            skLineSegment(sketch, "E6.12.1.1", {"start": v(233.75, 57.18) * mm, "end": v(236.5, 61.93) * mm});
            skLineSegment(sketch, "E6.12.1.2", {"start": v(236.5, 52.43) * mm, "end": v(233.75, 57.18) * mm});
            skLineSegment(sketch, "E6.12.1.3", {"start": v(241.98, 52.43) * mm, "end": v(236.5, 52.43) * mm});
            skLineSegment(sketch, "E6.12.1.4", {"start": v(244.72, 57.18) * mm, "end": v(241.98, 52.43) * mm});
            skLineSegment(sketch, "E6.12.1.5", {"start": v(243.36, 51.63) * mm, "end": v(246.1, 56.38) * mm});
            skLineSegment(sketch, "E6.12.1.6", {"start": v(246.1, 46.88) * mm, "end": v(243.36, 51.63) * mm});
            skLineSegment(sketch, "E6.12.1.7", {"start": v(251.59, 46.88) * mm, "end": v(246.1, 46.88) * mm});
            skLineSegment(sketch, "E6.12.1.8", {"start": v(254.33, 51.63) * mm, "end": v(251.59, 46.88) * mm});
            skLineSegment(sketch, "E6.12.1.9", {"start": v(251.59, 56.38) * mm, "end": v(254.33, 51.63) * mm});
            skLineSegment(sketch, "E6.12.1.10", {"start": v(246.1, 56.38) * mm, "end": v(251.59, 56.38) * mm});
            skLineSegment(sketch, "E6.12.1.11", {"start": v(236.5, 61.93) * mm, "end": v(241.98, 61.93) * mm});
            skLineSegment(sketch, "E6.12.2.0", {"start": v(241.98, 50.84) * mm, "end": v(244.72, 46.09) * mm});
            skLineSegment(sketch, "E6.12.2.1", {"start": v(233.75, 46.09) * mm, "end": v(236.5, 50.84) * mm});
            skLineSegment(sketch, "E6.12.2.2", {"start": v(236.5, 41.33) * mm, "end": v(233.75, 46.09) * mm});
            skLineSegment(sketch, "E6.12.2.3", {"start": v(241.98, 41.33) * mm, "end": v(236.5, 41.33) * mm});
            skLineSegment(sketch, "E6.12.2.4", {"start": v(244.72, 46.09) * mm, "end": v(241.98, 41.33) * mm});
            skLineSegment(sketch, "E6.12.2.5", {"start": v(243.36, 40.54) * mm, "end": v(246.1, 45.3) * mm});
            skLineSegment(sketch, "E6.12.2.6", {"start": v(246.1, 35.79) * mm, "end": v(243.36, 40.54) * mm});
            skLineSegment(sketch, "E6.12.2.7", {"start": v(251.59, 35.79) * mm, "end": v(246.1, 35.79) * mm});
            skLineSegment(sketch, "E6.12.2.8", {"start": v(254.33, 40.54) * mm, "end": v(251.59, 35.79) * mm});
            skLineSegment(sketch, "E6.12.2.9", {"start": v(251.59, 45.3) * mm, "end": v(254.33, 40.54) * mm});
            skLineSegment(sketch, "E6.12.2.10", {"start": v(246.1, 45.3) * mm, "end": v(251.59, 45.3) * mm});
            skLineSegment(sketch, "E6.12.2.11", {"start": v(236.5, 50.84) * mm, "end": v(241.98, 50.84) * mm});
            skLineSegment(sketch, "E6.12.3.0", {"start": v(241.98, 39.74) * mm, "end": v(244.72, 35) * mm});
            skLineSegment(sketch, "E6.12.3.1", {"start": v(233.75, 35) * mm, "end": v(236.5, 39.74) * mm});
            skLineSegment(sketch, "E6.12.3.2", {"start": v(236.5, 30.24) * mm, "end": v(233.75, 35) * mm});
            skLineSegment(sketch, "E6.12.3.3", {"start": v(241.98, 30.24) * mm, "end": v(236.5, 30.24) * mm});
            skLineSegment(sketch, "E6.12.3.4", {"start": v(244.72, 35) * mm, "end": v(241.98, 30.24) * mm});
            skLineSegment(sketch, "E6.12.3.5", {"start": v(243.36, 29.44) * mm, "end": v(246.1, 34.2) * mm});
            skLineSegment(sketch, "E6.12.3.6", {"start": v(246.1, 24.7) * mm, "end": v(243.36, 29.44) * mm});
            skLineSegment(sketch, "E6.12.3.7", {"start": v(251.59, 24.7) * mm, "end": v(246.1, 24.7) * mm});
            skLineSegment(sketch, "E6.12.3.8", {"start": v(254.33, 29.44) * mm, "end": v(251.59, 24.7) * mm});
            skLineSegment(sketch, "E6.12.3.9", {"start": v(251.59, 34.2) * mm, "end": v(254.33, 29.44) * mm});
            skLineSegment(sketch, "E6.12.3.10", {"start": v(246.1, 34.2) * mm, "end": v(251.59, 34.2) * mm});
            skLineSegment(sketch, "E6.12.3.11", {"start": v(236.5, 39.74) * mm, "end": v(241.98, 39.74) * mm});
            skLineSegment(sketch, "E6.12.4.0", {"start": v(241.98, 28.65) * mm, "end": v(244.72, 23.9) * mm});
            skLineSegment(sketch, "E6.12.4.1", {"start": v(233.75, 23.9) * mm, "end": v(236.5, 28.65) * mm});
            skLineSegment(sketch, "E6.12.4.2", {"start": v(236.5, 19.15) * mm, "end": v(233.75, 23.9) * mm});
            skLineSegment(sketch, "E6.12.4.3", {"start": v(241.98, 19.15) * mm, "end": v(236.5, 19.15) * mm});
            skLineSegment(sketch, "E6.12.4.4", {"start": v(244.72, 23.9) * mm, "end": v(241.98, 19.15) * mm});
            skLineSegment(sketch, "E6.12.4.5", {"start": v(243.36, 18.35) * mm, "end": v(246.1, 23.1) * mm});
            skLineSegment(sketch, "E6.12.4.6", {"start": v(246.1, 13.6) * mm, "end": v(243.36, 18.35) * mm});
            skLineSegment(sketch, "E6.12.4.7", {"start": v(251.59, 13.6) * mm, "end": v(246.1, 13.6) * mm});
            skLineSegment(sketch, "E6.12.4.8", {"start": v(254.33, 18.35) * mm, "end": v(251.59, 13.6) * mm});
            skLineSegment(sketch, "E6.12.4.9", {"start": v(251.59, 23.1) * mm, "end": v(254.33, 18.35) * mm});
            skLineSegment(sketch, "E6.12.4.10", {"start": v(246.1, 23.1) * mm, "end": v(251.59, 23.1) * mm});
            skLineSegment(sketch, "E6.12.4.11", {"start": v(236.5, 28.65) * mm, "end": v(241.98, 28.65) * mm});
            skLineSegment(sketch, "E6.12.5.0", {"start": v(241.98, 17.56) * mm, "end": v(244.72, 12.8) * mm});
            skLineSegment(sketch, "E6.12.5.1", {"start": v(233.75, 12.8) * mm, "end": v(236.5, 17.56) * mm});
            skLineSegment(sketch, "E6.12.5.2", {"start": v(236.5, 8.05) * mm, "end": v(233.75, 12.8) * mm});
            skLineSegment(sketch, "E6.12.5.3", {"start": v(241.98, 8.05) * mm, "end": v(236.5, 8.05) * mm});
            skLineSegment(sketch, "E6.12.5.4", {"start": v(244.72, 12.8) * mm, "end": v(241.98, 8.05) * mm});
            skLineSegment(sketch, "E6.12.5.5", {"start": v(243.36, 7.26) * mm, "end": v(246.1, 12.01) * mm});
            skLineSegment(sketch, "E6.12.5.6", {"start": v(246.1, 2.5) * mm, "end": v(243.36, 7.26) * mm});
            skLineSegment(sketch, "E6.12.5.7", {"start": v(251.59, 2.5) * mm, "end": v(246.1, 2.5) * mm});
            skLineSegment(sketch, "E6.12.5.8", {"start": v(254.33, 7.26) * mm, "end": v(251.59, 2.5) * mm});
            skLineSegment(sketch, "E6.12.5.9", {"start": v(251.59, 12.01) * mm, "end": v(254.33, 7.26) * mm});
            skLineSegment(sketch, "E6.12.5.10", {"start": v(246.1, 12.01) * mm, "end": v(251.59, 12.01) * mm});
            skLineSegment(sketch, "E6.12.5.11", {"start": v(236.5, 17.56) * mm, "end": v(241.98, 17.56) * mm});
            skLineSegment(sketch, "E6.direction1", {"start": v(5.92, 63.52) * mm, "end": v(25.13, 63.52) * mm, "construction": true});
            skLineSegment(sketch, "E6.direction2", {"start": v(5.92, 63.52) * mm, "end": v(5.92, 52.43) * mm, "construction": true});
            skLineSegment(sketch, "E7", {"start": v(13.24, 73.02) * mm, "end": v(15.53, 69.07) * mm});
            skLineSegment(sketch, "E8", {"start": v(15.53, 69.07) * mm, "end": v(21.01, 69.07) * mm});
            skLineSegment(sketch, "E9", {"start": v(21.01, 69.07) * mm, "end": v(23.3, 73.02) * mm});
            skPoint(sketch, "E10", {"position": v(18.27, 69.07) * mm});
            skLineSegment(sketch, "E11.1.0.0", {"start": v(32.45, 73.02) * mm, "end": v(34.74, 69.07) * mm});
            skLineSegment(sketch, "E11.1.0.1", {"start": v(34.74, 69.07) * mm, "end": v(40.23, 69.07) * mm});
            skLineSegment(sketch, "E11.1.0.2", {"start": v(40.23, 69.07) * mm, "end": v(42.51, 73.02) * mm});
            skLineSegment(sketch, "E11.2.0.0", {"start": v(51.67, 73.02) * mm, "end": v(53.96, 69.07) * mm});
            skLineSegment(sketch, "E11.2.0.1", {"start": v(53.96, 69.07) * mm, "end": v(59.44, 69.07) * mm});
            skLineSegment(sketch, "E11.2.0.2", {"start": v(59.44, 69.07) * mm, "end": v(61.73, 73.02) * mm});
            skLineSegment(sketch, "E11.3.0.0", {"start": v(70.88, 73.02) * mm, "end": v(73.17, 69.07) * mm});
            skLineSegment(sketch, "E11.3.0.1", {"start": v(73.17, 69.07) * mm, "end": v(78.66, 69.07) * mm});
            skLineSegment(sketch, "E11.3.0.2", {"start": v(78.66, 69.07) * mm, "end": v(80.94, 73.02) * mm});
            skLineSegment(sketch, "E11.4.0.0", {"start": v(90.1, 73.02) * mm, "end": v(92.38, 69.07) * mm});
            skLineSegment(sketch, "E11.4.0.1", {"start": v(92.38, 69.07) * mm, "end": v(97.87, 69.07) * mm});
            skLineSegment(sketch, "E11.4.0.2", {"start": v(97.87, 69.07) * mm, "end": v(100.16, 73.02) * mm});
            skLineSegment(sketch, "E11.5.0.0", {"start": v(109.31, 73.02) * mm, "end": v(111.6, 69.07) * mm});
            skLineSegment(sketch, "E11.5.0.1", {"start": v(111.6, 69.07) * mm, "end": v(117.09, 69.07) * mm});
            skLineSegment(sketch, "E11.5.0.2", {"start": v(117.09, 69.07) * mm, "end": v(119.37, 73.02) * mm});
            skLineSegment(sketch, "E11.6.0.0", {"start": v(128.53, 73.02) * mm, "end": v(130.81, 69.07) * mm});
            skLineSegment(sketch, "E11.6.0.1", {"start": v(130.81, 69.07) * mm, "end": v(136.3, 69.07) * mm});
            skLineSegment(sketch, "E11.6.0.2", {"start": v(136.3, 69.07) * mm, "end": v(138.59, 73.02) * mm});
            skLineSegment(sketch, "E11.7.0.0", {"start": v(147.74, 73.02) * mm, "end": v(150.03, 69.07) * mm});
            skLineSegment(sketch, "E11.7.0.1", {"start": v(150.03, 69.07) * mm, "end": v(155.52, 69.07) * mm});
            skLineSegment(sketch, "E11.7.0.2", {"start": v(155.52, 69.07) * mm, "end": v(157.8, 73.02) * mm});
            skLineSegment(sketch, "E11.8.0.0", {"start": v(166.96, 73.02) * mm, "end": v(169.24, 69.07) * mm});
            skLineSegment(sketch, "E11.8.0.1", {"start": v(169.24, 69.07) * mm, "end": v(174.73, 69.07) * mm});
            skLineSegment(sketch, "E11.8.0.2", {"start": v(174.73, 69.07) * mm, "end": v(177.02, 73.02) * mm});
            skLineSegment(sketch, "E11.9.0.0", {"start": v(186.17, 73.02) * mm, "end": v(188.46, 69.07) * mm});
            skLineSegment(sketch, "E11.9.0.1", {"start": v(188.46, 69.07) * mm, "end": v(193.94, 69.07) * mm});
            skLineSegment(sketch, "E11.9.0.2", {"start": v(193.94, 69.07) * mm, "end": v(196.23, 73.02) * mm});
            skLineSegment(sketch, "E11.10.0.0", {"start": v(205.38, 73.02) * mm, "end": v(207.67, 69.07) * mm});
            skLineSegment(sketch, "E11.10.0.1", {"start": v(207.67, 69.07) * mm, "end": v(213.16, 69.07) * mm});
            skLineSegment(sketch, "E11.10.0.2", {"start": v(213.16, 69.07) * mm, "end": v(215.44, 73.02) * mm});
            skLineSegment(sketch, "E11.11.0.0", {"start": v(224.6, 73.02) * mm, "end": v(226.89, 69.07) * mm});
            skLineSegment(sketch, "E11.11.0.1", {"start": v(226.89, 69.07) * mm, "end": v(232.37, 69.07) * mm});
            skLineSegment(sketch, "E11.11.0.2", {"start": v(232.37, 69.07) * mm, "end": v(234.66, 73.02) * mm});
            skLineSegment(sketch, "E11.12.0.0", {"start": v(243.81, 73.02) * mm, "end": v(246.1, 69.07) * mm});
            skLineSegment(sketch, "E11.12.0.1", {"start": v(246.1, 69.07) * mm, "end": v(251.59, 69.07) * mm});
            skLineSegment(sketch, "E11.12.0.2", {"start": v(251.59, 69.07) * mm, "end": v(253.87, 73.02) * mm});
            skLineSegment(sketch, "E11.direction1", {"start": v(15.53, 69.07) * mm, "end": v(34.74, 69.07) * mm, "construction": true});
            skLineSegment(sketch, "E12", {"start": v(13.37, 2.52) * mm, "end": v(11.3, 6.22) * mm});
            skLineSegment(sketch, "E13", {"start": v(11.3, 6.22) * mm, "end": v(5.8, 6.22) * mm});
            skLineSegment(sketch, "E14", {"start": v(5.8, 6.22) * mm, "end": v(3.08, 2.4) * mm});
            skSolve(sketch);
        }
        {
            var Q0;
            {var subQ136=sQuery(id+"F0.wireOp",EDGE,"E2.1");Q0=makeQuery(id+"F0.imprint","IMPRINT",FACE,{"disambiguationData":[TD([[makeQuery(id+"F0.imprint","IMPRINT",EDGE,{"derivedFrom":subQ136}),1.0]])]});}
            var Q1;
            {var subQ64=sQuery(id+"F0.wireOp",EDGE,"E0.bottom");Q1=makeQuery(id+"F0.imprint","IMPRINT",FACE,{"disambiguationData":[TD([[makeQuery(id+"F0.imprint","IMPRINT",EDGE,{"derivedFrom":subQ64}),1.0]])]});}
            var Q2;
            {var subQ3=sQuery(id+"F0.wireOp",EDGE,"E0.right");var subQ8=sQuery(id+"F0.wireOp",EDGE,"E6.12.5.9");var subQ10=makeQuery(id+"F0.imprint","INTERSECT",VERTEX,{"derivedFrom":[subQ3,subQ8]});Q2=makeQuery(id+"F0.imprint","IMPRINT",FACE,{"disambiguationData":[TD([[makeQuery(id+"F0.imprint","IMPRINT",EDGE,{"disambiguationData":[TD([[subQ10,-1.0]])],"derivedFrom":subQ3}),1.0]])]});}
            var Q3;
            {var subQ0=sQuery(id+"F0.wireOp",EDGE,"E6.12.5.7");Q3=makeQuery(id+"F0.imprint","IMPRINT",FACE,{"disambiguationData":[TD([[makeQuery(id+"F0.imprint","IMPRINT",EDGE,{"derivedFrom":subQ0}),-1.0]])]});}
            var Q4;
            {var subQ0=sQuery(id+"F0.wireOp",EDGE,"E6.12.4.8");var subQ3=sQuery(id+"F0.wireOp",EDGE,"E0.right");var subQ4=makeQuery(id+"F0.imprint","INTERSECT",VERTEX,{"derivedFrom":[subQ3,subQ0]});Q4=makeQuery(id+"F0.imprint","IMPRINT",FACE,{"disambiguationData":[TD([[makeQuery(id+"F0.imprint","IMPRINT",EDGE,{"disambiguationData":[TD([[subQ4,-1.0]])],"derivedFrom":subQ3}),1.0]])]});}
            var Q5;
            {var subQ3=sQuery(id+"F0.wireOp",EDGE,"E0.right");var subQ9=sQuery(id+"F0.wireOp",EDGE,"E6.12.4.9");var subQ11=makeQuery(id+"F0.imprint","INTERSECT",VERTEX,{"derivedFrom":[subQ3,subQ9]});Q5=makeQuery(id+"F0.imprint","IMPRINT",FACE,{"disambiguationData":[TD([[makeQuery(id+"F0.imprint","IMPRINT",EDGE,{"disambiguationData":[TD([[subQ11,-1.0]])],"derivedFrom":subQ3}),1.0]])]});}
            var Q6;
            {var subQ0=sQuery(id+"F0.wireOp",EDGE,"E6.12.3.8");var subQ3=sQuery(id+"F0.wireOp",EDGE,"E0.right");var subQ4=makeQuery(id+"F0.imprint","INTERSECT",VERTEX,{"derivedFrom":[subQ3,subQ0]});Q6=makeQuery(id+"F0.imprint","IMPRINT",FACE,{"disambiguationData":[TD([[makeQuery(id+"F0.imprint","IMPRINT",EDGE,{"disambiguationData":[TD([[subQ4,-1.0]])],"derivedFrom":subQ3}),1.0]])]});}
            var Q7;
            {var subQ3=sQuery(id+"F0.wireOp",EDGE,"E0.right");var subQ9=sQuery(id+"F0.wireOp",EDGE,"E6.12.3.9");var subQ11=makeQuery(id+"F0.imprint","INTERSECT",VERTEX,{"derivedFrom":[subQ3,subQ9]});Q7=makeQuery(id+"F0.imprint","IMPRINT",FACE,{"disambiguationData":[TD([[makeQuery(id+"F0.imprint","IMPRINT",EDGE,{"disambiguationData":[TD([[subQ11,-1.0]])],"derivedFrom":subQ3}),1.0]])]});}
            var Q8;
            {var subQ0=sQuery(id+"F0.wireOp",EDGE,"E6.12.2.8");var subQ3=sQuery(id+"F0.wireOp",EDGE,"E0.right");var subQ4=makeQuery(id+"F0.imprint","INTERSECT",VERTEX,{"derivedFrom":[subQ3,subQ0]});Q8=makeQuery(id+"F0.imprint","IMPRINT",FACE,{"disambiguationData":[TD([[makeQuery(id+"F0.imprint","IMPRINT",EDGE,{"disambiguationData":[TD([[subQ4,-1.0]])],"derivedFrom":subQ3}),1.0]])]});}
            var Q9;
            {var subQ3=sQuery(id+"F0.wireOp",EDGE,"E0.right");var subQ9=sQuery(id+"F0.wireOp",EDGE,"E6.12.2.9");var subQ10=makeQuery(id+"F0.imprint","INTERSECT",VERTEX,{"derivedFrom":[subQ3,subQ9]});Q9=makeQuery(id+"F0.imprint","IMPRINT",FACE,{"disambiguationData":[TD([[makeQuery(id+"F0.imprint","IMPRINT",EDGE,{"disambiguationData":[TD([[subQ10,-1.0]])],"derivedFrom":subQ3}),1.0]])]});}
            var Q10;
            {var subQ0=sQuery(id+"F0.wireOp",EDGE,"E6.12.1.8");var subQ9=sQuery(id+"F0.wireOp",EDGE,"E0.right");var subQ10=makeQuery(id+"F0.imprint","INTERSECT",VERTEX,{"derivedFrom":[subQ9,subQ0]});Q10=makeQuery(id+"F0.imprint","IMPRINT",FACE,{"disambiguationData":[TD([[makeQuery(id+"F0.imprint","IMPRINT",EDGE,{"disambiguationData":[TD([[subQ10,-1.0]])],"derivedFrom":subQ9}),1.0]])]});}
            var Q11;
            {var subQ5=sQuery(id+"F0.wireOp",EDGE,"E0.right");var subQ9=sQuery(id+"F0.wireOp",EDGE,"E6.12.1.9");var subQ11=makeQuery(id+"F0.imprint","INTERSECT",VERTEX,{"derivedFrom":[subQ5,subQ9]});Q11=makeQuery(id+"F0.imprint","IMPRINT",FACE,{"disambiguationData":[TD([[makeQuery(id+"F0.imprint","IMPRINT",EDGE,{"disambiguationData":[TD([[subQ11,-1.0]])],"derivedFrom":subQ5}),1.0]])]});}
            var Q12;
            {var subQ0=sQuery(id+"F0.wireOp",EDGE,"E6.12.0.8");var subQ9=sQuery(id+"F0.wireOp",EDGE,"E0.right");var subQ10=makeQuery(id+"F0.imprint","INTERSECT",VERTEX,{"derivedFrom":[subQ9,subQ0]});Q12=makeQuery(id+"F0.imprint","IMPRINT",FACE,{"disambiguationData":[TD([[makeQuery(id+"F0.imprint","IMPRINT",EDGE,{"disambiguationData":[TD([[subQ10,-1.0]])],"derivedFrom":subQ9}),1.0]])]});}
            var Q13;
            {var subQ5=sQuery(id+"F0.wireOp",EDGE,"E6.0.5.7");Q13=makeQuery(id+"F0.imprint","IMPRINT",FACE,{"disambiguationData":[TD([[makeQuery(id+"F0.imprint","IMPRINT",EDGE,{"derivedFrom":subQ5}),-1.0]])]});}
            var Q14;
            {var subQ5=sQuery(id+"F0.wireOp",EDGE,"E6.1.5.7");Q14=makeQuery(id+"F0.imprint","IMPRINT",FACE,{"disambiguationData":[TD([[makeQuery(id+"F0.imprint","IMPRINT",EDGE,{"derivedFrom":subQ5}),-1.0]])]});}
            var Q15;
            {var subQ5=sQuery(id+"F0.wireOp",EDGE,"E6.2.5.7");Q15=makeQuery(id+"F0.imprint","IMPRINT",FACE,{"disambiguationData":[TD([[makeQuery(id+"F0.imprint","IMPRINT",EDGE,{"derivedFrom":subQ5}),-1.0]])]});}
            var Q16;
            {var subQ5=sQuery(id+"F0.wireOp",EDGE,"E6.3.5.7");Q16=makeQuery(id+"F0.imprint","IMPRINT",FACE,{"disambiguationData":[TD([[makeQuery(id+"F0.imprint","IMPRINT",EDGE,{"derivedFrom":subQ5}),-1.0]])]});}
            var Q17;
            {var subQ5=sQuery(id+"F0.wireOp",EDGE,"E6.4.5.7");Q17=makeQuery(id+"F0.imprint","IMPRINT",FACE,{"disambiguationData":[TD([[makeQuery(id+"F0.imprint","IMPRINT",EDGE,{"derivedFrom":subQ5}),-1.0]])]});}
            var Q18;
            {var subQ5=sQuery(id+"F0.wireOp",EDGE,"E6.5.5.7");Q18=makeQuery(id+"F0.imprint","IMPRINT",FACE,{"disambiguationData":[TD([[makeQuery(id+"F0.imprint","IMPRINT",EDGE,{"derivedFrom":subQ5}),-1.0]])]});}
            var Q19;
            {var subQ5=sQuery(id+"F0.wireOp",EDGE,"E6.6.5.7");Q19=makeQuery(id+"F0.imprint","IMPRINT",FACE,{"disambiguationData":[TD([[makeQuery(id+"F0.imprint","IMPRINT",EDGE,{"derivedFrom":subQ5}),-1.0]])]});}
            var Q20;
            {var subQ5=sQuery(id+"F0.wireOp",EDGE,"E6.7.5.7");Q20=makeQuery(id+"F0.imprint","IMPRINT",FACE,{"disambiguationData":[TD([[makeQuery(id+"F0.imprint","IMPRINT",EDGE,{"derivedFrom":subQ5}),-1.0]])]});}
            var Q21;
            {var subQ5=sQuery(id+"F0.wireOp",EDGE,"E6.8.5.7");Q21=makeQuery(id+"F0.imprint","IMPRINT",FACE,{"disambiguationData":[TD([[makeQuery(id+"F0.imprint","IMPRINT",EDGE,{"derivedFrom":subQ5}),-1.0]])]});}
            var Q22;
            {var subQ5=sQuery(id+"F0.wireOp",EDGE,"E6.9.5.7");Q22=makeQuery(id+"F0.imprint","IMPRINT",FACE,{"disambiguationData":[TD([[makeQuery(id+"F0.imprint","IMPRINT",EDGE,{"derivedFrom":subQ5}),-1.0]])]});}
            var Q23;
            {var subQ5=sQuery(id+"F0.wireOp",EDGE,"E6.10.5.7");Q23=makeQuery(id+"F0.imprint","IMPRINT",FACE,{"disambiguationData":[TD([[makeQuery(id+"F0.imprint","IMPRINT",EDGE,{"derivedFrom":subQ5}),-1.0]])]});}
            var Q24;
            {var subQ5=sQuery(id+"F0.wireOp",EDGE,"E6.11.5.7");Q24=makeQuery(id+"F0.imprint","IMPRINT",FACE,{"disambiguationData":[TD([[makeQuery(id+"F0.imprint","IMPRINT",EDGE,{"derivedFrom":subQ5}),-1.0]])]});}
            extrude(context, id + "F1", {"entities" : qUnion([Q0, Q1, Q2, Q3, Q4, Q5, Q6, Q7, Q8, Q9, Q10, Q11, Q12, Q13, Q14, Q15, Q16, Q17, Q18, Q19, Q20, Q21, Q22, Q23, Q24]), "depth" : 12.7 * mm});
        }
    });
